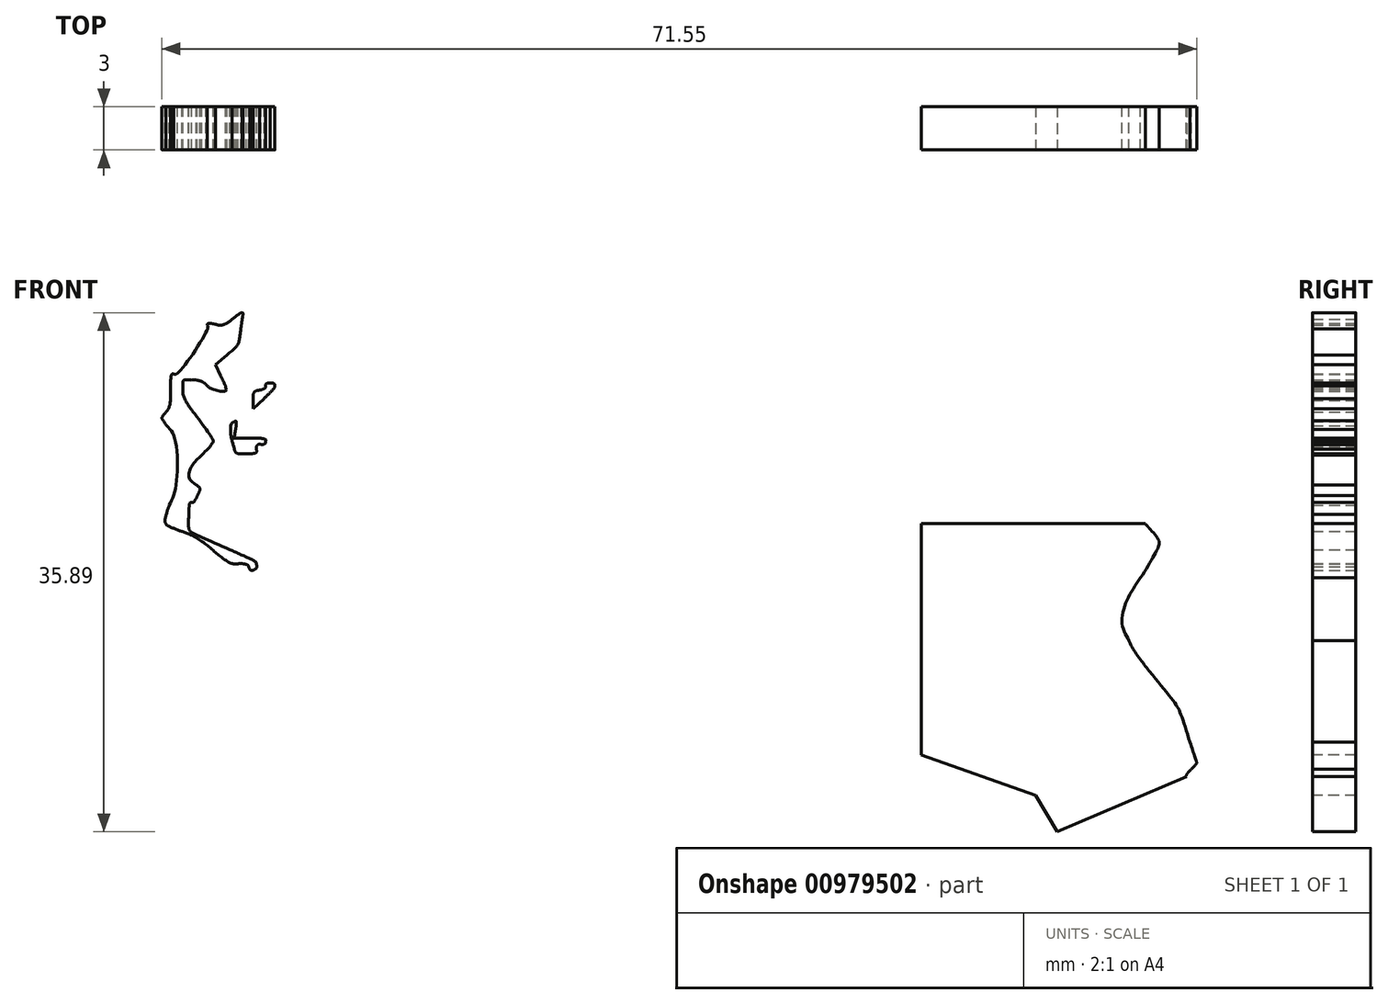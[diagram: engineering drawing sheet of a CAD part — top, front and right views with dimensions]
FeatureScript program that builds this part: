
annotation { "Feature Type Name" : "Feature", "Feature Type Description" : "" }
export const myFeature = defineFeature(function(context is Context, id is Id, definition is map)
    precondition{}
    {
        {
            var Q0;
            Q0=qCreatedBy(makeId("Front.planeOp"),FACE);
            var sketch = newSketch(context, id + "F0", { "sketchPlane" : qUnion([Q0])});
            skLineSegment(sketch, "E0", {"start": v(-32.88, 19.2) * mm, "end": v(-32.1, 20.83) * mm});
            skLineSegment(sketch, "E1", {"start": v(-32.1, 20.83) * mm, "end": v(-32.57, 22.16) * mm});
            skLineSegment(sketch, "E2", {"start": v(-27.5, 16.63) * mm, "end": v(-26.83, 16.28) * mm});
            skLineSegment(sketch, "E3", {"start": v(-26.83, 16.28) * mm, "end": v(-26.97, 16.83) * mm});
            skLineSegment(sketch, "E4", {"start": v(-24.85, 15.67) * mm, "end": v(-25.4, 15.88) * mm});
            skLineSegment(sketch, "E5", {"start": v(-25.4, 15.88) * mm, "end": v(-25.34, 18.4) * mm});
            skLineSegment(sketch, "E6", {"start": v(-1.75, 78.04) * mm, "end": v(-0.2, 79.6) * mm});
            skLineSegment(sketch, "E7", {"start": v(-0.2, 79.6) * mm, "end": v(1.27, 79.6) * mm});
            skLineSegment(sketch, "E8", {"start": v(38.3, 44.26) * mm, "end": v(38.3, 43.17) * mm});
            skLineSegment(sketch, "E9", {"start": v(38.3, 43.17) * mm, "end": v(37.62, 43.24) * mm});
            skLineSegment(sketch, "E10", {"start": v(39.65, -31.25) * mm, "end": v(39.52, -33.83) * mm});
            skLineSegment(sketch, "E11", {"start": v(39.52, -33.83) * mm, "end": v(40.18, -34.42) * mm});
            skLineSegment(sketch, "E12", {"start": v(1.4, 79.08) * mm, "end": v(0.3, 79.22) * mm});
            skLineSegment(sketch, "E13", {"start": v(0.3, 79.22) * mm, "end": v(-1.23, 77.67) * mm});
            skLineSegment(sketch, "E14", {"start": v(-12.51, 69.45) * mm, "end": v(-13.4, 69.45) * mm});
            skLineSegment(sketch, "E15", {"start": v(-13.4, 69.45) * mm, "end": v(-13.27, 67.07) * mm});
            skLineSegment(sketch, "E16", {"start": v(-18.31, 54.9) * mm, "end": v(-18.88, 53.48) * mm});
            skLineSegment(sketch, "E17", {"start": v(-18.88, 53.48) * mm, "end": v(-18.43, 53.1) * mm});
            skLineSegment(sketch, "E18", {"start": v(-20.94, 40.45) * mm, "end": v(-21.55, 40.45) * mm});
            skLineSegment(sketch, "E19", {"start": v(-21.55, 40.45) * mm, "end": v(-21.44, 41.8) * mm});
            skLineSegment(sketch, "E20", {"start": v(-24.47, 43.3) * mm, "end": v(-25.23, 42.61) * mm});
            skLineSegment(sketch, "E21", {"start": v(-25.23, 42.61) * mm, "end": v(-24.8, 41.05) * mm});
            skLineSegment(sketch, "E22", {"start": v(-37.96, -16.18) * mm, "end": v(-37.29, -17.23) * mm});
            skLineSegment(sketch, "E23", {"start": v(-37.29, -17.23) * mm, "end": v(-37.41, -20.41) * mm});
            skLineSegment(sketch, "E24", {"start": v(-30.4, -60.92) * mm, "end": v(-31.42, -62.04) * mm});
            skLineSegment(sketch, "E25", {"start": v(-31.42, -62.04) * mm, "end": v(-30.9, -63.02) * mm});
            skLineSegment(sketch, "E26", {"start": v(-36.35, 33.14) * mm, "end": v(-36.7, 33.88) * mm});
            skLineSegment(sketch, "E27", {"start": v(-36.7, 33.88) * mm, "end": v(-35.92, 34.57) * mm});
            skLineSegment(sketch, "E28", {"start": v(-34.09, 31.43) * mm, "end": v(-34.09, 30.84) * mm});
            skLineSegment(sketch, "E29", {"start": v(-34.09, 30.84) * mm, "end": v(-33.35, 31.56) * mm});
            skFitSpline(sketch, "E30", {"points": [v(-13.45, -80.7) * mm, v(-14.26, -80.4) * mm, v(-15.79, -79.86) * mm, v(-16.84, -79.51) * mm]});
            skFitSpline(sketch, "E31", {"points": [v(-16.84, -79.51) * mm, v(-20.43, -78.33) * mm, v(-20.6, -78.25) * mm, v(-21.55, -77.26) * mm]});
            skFitSpline(sketch, "E32", {"points": [v(-21.55, -77.26) * mm, v(-22.07, -76.72) * mm, v(-23.66, -74.52) * mm, v(-25.09, -72.37) * mm]});
            skFitSpline(sketch, "E33", {"points": [v(-25.09, -72.37) * mm, v(-26.52, -70.21) * mm, v(-28.36, -67.6) * mm, v(-29.19, -66.55) * mm]});
            skFitSpline(sketch, "E34", {"points": [v(-29.19, -66.55) * mm, v(-30.6, -64.76) * mm, v(-31.97, -62.53) * mm, v(-31.97, -62.03) * mm]});
            skFitSpline(sketch, "E35", {"points": [v(-31.97, -62.03) * mm, v(-31.97, -61.91) * mm, v(-31.5, -61.27) * mm, v(-30.92, -60.6) * mm]});
            skFitSpline(sketch, "E36", {"points": [v(-30.92, -60.6) * mm, v(-29.85, -59.39) * mm, v(-29, -57.92) * mm, v(-29, -57.28) * mm]});
            skFitSpline(sketch, "E37", {"points": [v(-29, -57.28) * mm, v(-29, -57.08) * mm, v(-29.34, -56.3) * mm, v(-29.75, -55.53) * mm]});
            skFitSpline(sketch, "E38", {"points": [v(-29.75, -55.53) * mm, v(-30.57, -53.98) * mm, v(-30.63, -53.57) * mm, v(-30.2, -52.72) * mm]});
            skFitSpline(sketch, "E39", {"points": [v(-30.2, -52.72) * mm, v(-29.95, -52.26) * mm, v(-29.92, -51.55) * mm, v(-30.04, -49.29) * mm]});
            skFitSpline(sketch, "E40", {"points": [v(-30.04, -49.29) * mm, v(-30.2, -46.13) * mm, v(-30.12, -46.32) * mm, v(-32.34, -43.6) * mm]});
            skFitSpline(sketch, "E41", {"points": [v(-32.34, -43.6) * mm, v(-32.83, -43) * mm, v(-33.38, -42.01) * mm, v(-33.55, -41.42) * mm]});
            skFitSpline(sketch, "E42", {"points": [v(-33.55, -41.42) * mm, v(-33.73, -40.84) * mm, v(-34.2, -39.94) * mm, v(-34.62, -39.44) * mm]});
            skFitSpline(sketch, "E43", {"points": [v(-34.62, -39.44) * mm, v(-36.03, -37.71) * mm, v(-36.52, -35.97) * mm, v(-35.98, -34.56) * mm]});
            skFitSpline(sketch, "E44", {"points": [v(-35.98, -34.56) * mm, v(-35.86, -34.24) * mm, v(-35.38, -33.57) * mm, v(-34.92, -33.07) * mm]});
            skFitSpline(sketch, "E45", {"points": [v(-34.92, -33.07) * mm, v(-33.97, -32.03) * mm, v(-34, -32.17) * mm, v(-34.37, -30.78) * mm]});
            skFitSpline(sketch, "E46", {"points": [v(-34.37, -30.78) * mm, v(-34.75, -29.38) * mm, v(-35.2, -28.53) * mm, v(-36.46, -26.88) * mm]});
            skFitSpline(sketch, "E47", {"points": [v(-36.46, -26.88) * mm, v(-37.04, -26.13) * mm, v(-37.61, -25.27) * mm, v(-37.73, -24.97) * mm]});
            skFitSpline(sketch, "E48", {"points": [v(-37.73, -24.97) * mm, v(-37.97, -24.39) * mm, v(-38.06, -21.07) * mm, v(-37.9, -18.8) * mm]});
            skFitSpline(sketch, "E49", {"points": [v(-37.9, -18.8) * mm, v(-37.82, -17.55) * mm, v(-37.87, -17.35) * mm, v(-38.39, -16.67) * mm]});
            skFitSpline(sketch, "E50", {"points": [v(-38.39, -16.67) * mm, v(-39.51, -15.19) * mm, v(-39.6, -12.77) * mm, v(-38.72, -7.81) * mm]});
            skFitSpline(sketch, "E51", {"points": [v(-38.72, -7.81) * mm, v(-38.24, -5.14) * mm, v(-38.31, -2.1) * mm, v(-38.87, -1) * mm]});
            skFitSpline(sketch, "E52", {"points": [v(-38.87, -1) * mm, v(-39.1, -0.56) * mm, v(-39.11, -0.29) * mm, v(-38.94, 0.17) * mm]});
            skFitSpline(sketch, "E53", {"points": [v(-38.94, 0.17) * mm, v(-38.62, 1) * mm, v(-38.87, 3.38) * mm, v(-39.5, 5.38) * mm]});
            skFitSpline(sketch, "E54", {"points": [v(-39.5, 5.38) * mm, v(-39.78, 6.29) * mm, v(-40.01, 7.26) * mm, v(-40.01, 7.54) * mm]});
            skFitSpline(sketch, "E55", {"points": [v(-40.01, 7.54) * mm, v(-40.01, 7.83) * mm, v(-39.68, 9.05) * mm, v(-39.27, 10.27) * mm]});
            skFitSpline(sketch, "E56", {"points": [v(-39.27, 10.27) * mm, v(-38.41, 12.85) * mm, v(-38.39, 13.06) * mm, v(-38.96, 13.2) * mm]});
            skFitSpline(sketch, "E57", {"points": [v(-38.96, 13.2) * mm, v(-39.71, 13.4) * mm, v(-39.48, 14.32) * mm, v(-38.38, 15.5) * mm]});
            skFitSpline(sketch, "E58", {"points": [v(-38.38, 15.5) * mm, v(-36.83, 17.16) * mm, v(-35.68, 17.57) * mm, v(-34.74, 16.8) * mm]});
            skFitSpline(sketch, "E59", {"points": [v(-34.74, 16.8) * mm, v(-34.08, 16.26) * mm, v(-32.77, 13.22) * mm, v(-32.66, 11.98) * mm]});
            skFitSpline(sketch, "E60", {"points": [v(-32.66, 11.98) * mm, v(-32.55, 10.86) * mm, v(-32.37, 10.61) * mm, v(-31.6, 10.6) * mm]});
            skFitSpline(sketch, "E61", {"points": [v(-31.6, 10.6) * mm, v(-31, 10.6) * mm, v(-30.96, 11.24) * mm, v(-31.55, 11.77) * mm]});
            skFitSpline(sketch, "E62", {"points": [v(-31.55, 11.77) * mm, v(-31.84, 12.03) * mm, v(-31.97, 12.42) * mm, v(-31.97, 13) * mm]});
            skFitSpline(sketch, "E63", {"points": [v(-31.97, 13) * mm, v(-31.97, 14.32) * mm, v(-32.62, 16.12) * mm, v(-33.18, 16.38) * mm]});
            skFitSpline(sketch, "E64", {"points": [v(-33.18, 16.38) * mm, v(-33.86, 16.69) * mm, v(-33.8, 17.27) * mm, v(-32.88, 19.2) * mm]});
            skFitSpline(sketch, "E65", {"points": [v(-32.57, 22.16) * mm, v(-32.82, 22.9) * mm, v(-33.03, 23.65) * mm, v(-33.03, 23.83) * mm]});
            skFitSpline(sketch, "E66", {"points": [v(-33.03, 23.83) * mm, v(-33.03, 24.1) * mm, v(-33.14, 24.14) * mm, v(-33.5, 24.01) * mm]});
            skFitSpline(sketch, "E67", {"points": [v(-33.5, 24.01) * mm, v(-33.77, 23.92) * mm, v(-34.4, 23.84) * mm, v(-34.93, 23.84) * mm]});
            skFitSpline(sketch, "E68", {"points": [v(-34.93, 23.84) * mm, v(-35.84, 23.83) * mm, v(-35.89, 23.86) * mm, v(-35.95, 24.48) * mm]});
            skFitSpline(sketch, "E69", {"points": [v(-35.95, 24.48) * mm, v(-36.05, 25.55) * mm, v(-34.78, 26.27) * mm, v(-32.78, 26.27) * mm]});
            skFitSpline(sketch, "E70", {"points": [v(-32.78, 26.27) * mm, v(-31.93, 26.27) * mm, v(-31.64, 26.16) * mm, v(-31.1, 25.65) * mm]});
            skFitSpline(sketch, "E71", {"points": [v(-31.1, 25.65) * mm, v(-30.75, 25.3) * mm, v(-30.32, 25.08) * mm, v(-30.15, 25.14) * mm]});
            skFitSpline(sketch, "E72", {"points": [v(-30.15, 25.14) * mm, v(-29.7, 25.31) * mm, v(-29.77, 25.47) * mm, v(-30.7, 26.37) * mm]});
            skFitSpline(sketch, "E73", {"points": [v(-30.7, 26.37) * mm, v(-31.5, 27.15) * mm, v(-31.55, 27.27) * mm, v(-31.55, 28.43) * mm]});
            skFitSpline(sketch, "E74", {"points": [v(-31.55, 28.43) * mm, v(-31.55, 29.6) * mm, v(-31.52, 29.65) * mm, v(-31.02, 29.65) * mm]});
            skFitSpline(sketch, "E75", {"points": [v(-31.02, 29.65) * mm, v(-30.7, 29.65) * mm, v(-30.49, 29.53) * mm, v(-30.49, 29.36) * mm]});
            skFitSpline(sketch, "E76", {"points": [v(-30.49, 29.36) * mm, v(-30.49, 28.94) * mm, v(-28.82, 27.75) * mm, v(-28.24, 27.75) * mm]});
            skFitSpline(sketch, "E77", {"points": [v(-28.24, 27.75) * mm, v(-27.83, 27.75) * mm, v(-27.75, 27.6) * mm, v(-27.62, 26.6) * mm]});
            skFitSpline(sketch, "E78", {"points": [v(-27.62, 26.6) * mm, v(-27.46, 25.26) * mm, v(-27.66, 24.55) * mm, v(-28.57, 23.22) * mm]});
            skFitSpline(sketch, "E79", {"points": [v(-28.57, 23.22) * mm, v(-29.21, 22.29) * mm, v(-29.4, 21.61) * mm, v(-29.02, 21.61) * mm]});
            skFitSpline(sketch, "E80", {"points": [v(-29.02, 21.61) * mm, v(-28.66, 21.61) * mm, v(-28.35, 20.18) * mm, v(-28.49, 19.14) * mm]});
            skFitSpline(sketch, "E81", {"points": [v(-28.49, 19.14) * mm, v(-28.66, 17.84) * mm, v(-28.36, 17.07) * mm, v(-27.5, 16.63) * mm]});
            skFitSpline(sketch, "E82", {"points": [v(-26.97, 16.83) * mm, v(-27.1, 17.33) * mm, v(-27.05, 17.38) * mm, v(-26.5, 17.38) * mm]});
            skFitSpline(sketch, "E83", {"points": [v(-26.5, 17.38) * mm, v(-25.81, 17.38) * mm, v(-25.62, 17.08) * mm, v(-25.62, 16.04) * mm]});
            skFitSpline(sketch, "E84", {"points": [v(-25.62, 16.04) * mm, v(-25.62, 15.5) * mm, v(-25.82, 15.19) * mm, v(-26.56, 14.52) * mm]});
            skFitSpline(sketch, "E85", {"points": [v(-26.56, 14.52) * mm, v(-27.09, 14.05) * mm, v(-27.58, 13.4) * mm, v(-27.66, 13.06) * mm]});
            skFitSpline(sketch, "E86", {"points": [v(-27.66, 13.06) * mm, v(-27.79, 12.49) * mm, v(-27.76, 12.45) * mm, v(-27.3, 12.58) * mm]});
            skFitSpline(sketch, "E87", {"points": [v(-27.3, 12.58) * mm, v(-27.01, 12.65) * mm, v(-26.47, 12.72) * mm, v(-26.09, 12.72) * mm]});
            skFitSpline(sketch, "E88", {"points": [v(-26.09, 12.72) * mm, v(-25.47, 12.72) * mm, v(-25.42, 12.76) * mm, v(-25.61, 13.13) * mm]});
            skFitSpline(sketch, "E89", {"points": [v(-25.61, 13.13) * mm, v(-26.02, 13.88) * mm, v(-25.88, 14.6) * mm, v(-25.31, 14.75) * mm]});
            skFitSpline(sketch, "E90", {"points": [v(-25.31, 14.75) * mm, v(-25.03, 14.82) * mm, v(-24.68, 15.01) * mm, v(-24.55, 15.17) * mm]});
            skFitSpline(sketch, "E91", {"points": [v(-24.55, 15.17) * mm, v(-24.35, 15.4) * mm, v(-24.42, 15.5) * mm, v(-24.85, 15.67) * mm]});
            skFitSpline(sketch, "E92", {"points": [v(-25.34, 18.4) * mm, v(-25.28, 20.49) * mm, v(-25.2, 21.05) * mm, v(-24.84, 21.66) * mm]});
            skFitSpline(sketch, "E93", {"points": [v(-24.84, 21.66) * mm, v(-24.6, 22.07) * mm, v(-24.33, 22.91) * mm, v(-24.25, 23.54) * mm]});
            skFitSpline(sketch, "E94", {"points": [v(-24.25, 23.54) * mm, v(-24.05, 24.98) * mm, v(-23.67, 25.42) * mm, v(-22.64, 25.42) * mm]});
            skFitSpline(sketch, "E95", {"points": [v(-22.64, 25.42) * mm, v(-21.97, 25.42) * mm, v(-21.73, 25.28) * mm, v(-21.09, 24.54) * mm]});
            skFitSpline(sketch, "E96", {"points": [v(-21.09, 24.54) * mm, v(-20.67, 24.05) * mm, v(-20.32, 23.55) * mm, v(-20.32, 23.43) * mm]});
            skFitSpline(sketch, "E97", {"points": [v(-20.32, 23.43) * mm, v(-20.3, 22.93) * mm, v(-19.5, 25.15) * mm, v(-19.5, 25.74) * mm]});
            skFitSpline(sketch, "E98", {"points": [v(-19.5, 25.74) * mm, v(-19.48, 26.68) * mm, v(-19.75, 27) * mm, v(-20.27, 26.68) * mm]});
            skFitSpline(sketch, "E99", {"points": [v(-20.27, 26.68) * mm, v(-20.84, 26.32) * mm, v(-23.7, 26.75) * mm, v(-24.99, 27.38) * mm]});
            skFitSpline(sketch, "E100", {"points": [v(-24.99, 27.38) * mm, v(-26.7, 28.23) * mm, v(-27.27, 29.95) * mm, v(-26.55, 32.07) * mm]});
            skFitSpline(sketch, "E101", {"points": [v(-26.55, 32.07) * mm, v(-26.23, 33) * mm, v(-26.23, 33.13) * mm, v(-26.58, 33.9) * mm]});
            skFitSpline(sketch, "E102", {"points": [v(-26.58, 33.9) * mm, v(-27.04, 34.91) * mm, v(-26.9, 36) * mm, v(-26.2, 36.92) * mm]});
            skFitSpline(sketch, "E103", {"points": [v(-26.2, 36.92) * mm, v(-24.96, 38.54) * mm, v(-24.76, 39.42) * mm, v(-25.3, 40.73) * mm]});
            skFitSpline(sketch, "E104", {"points": [v(-25.3, 40.73) * mm, v(-25.48, 41.15) * mm, v(-25.62, 41.87) * mm, v(-25.62, 42.33) * mm]});
            skFitSpline(sketch, "E105", {"points": [v(-25.62, 42.33) * mm, v(-25.62, 43.02) * mm, v(-25.5, 43.25) * mm, v(-24.99, 43.62) * mm]});
            skFitSpline(sketch, "E106", {"points": [v(-24.99, 43.62) * mm, v(-24.64, 43.87) * mm, v(-24.35, 44.26) * mm, v(-24.35, 44.48) * mm]});
            skFitSpline(sketch, "E107", {"points": [v(-24.35, 44.48) * mm, v(-24.35, 45.6) * mm, v(-22.43, 46.16) * mm, v(-21.62, 45.29) * mm]});
            skFitSpline(sketch, "E108", {"points": [v(-21.62, 45.29) * mm, v(-21.1, 44.74) * mm, v(-20.66, 42.78) * mm, v(-20.82, 41.8) * mm]});
            skFitSpline(sketch, "E109", {"points": [v(-20.82, 41.8) * mm, v(-20.95, 40.98) * mm, v(-20.5, 40.8) * mm, v(-20.12, 41.5) * mm]});
            skFitSpline(sketch, "E110", {"points": [v(-20.12, 41.5) * mm, v(-20, 41.74) * mm, v(-19.7, 41.93) * mm, v(-19.48, 41.93) * mm]});
            skFitSpline(sketch, "E111", {"points": [v(-19.48, 41.93) * mm, v(-19.2, 41.93) * mm, v(-19.03, 42.12) * mm, v(-18.95, 42.51) * mm]});
            skFitSpline(sketch, "E112", {"points": [v(-18.95, 42.51) * mm, v(-18.9, 42.83) * mm, v(-18.75, 43.5) * mm, v(-18.63, 44) * mm]});
            skFitSpline(sketch, "E113", {"points": [v(-18.63, 44) * mm, v(-18.15, 46.1) * mm, v(-18.46, 46.83) * mm, v(-19.95, 47.1) * mm]});
            skFitSpline(sketch, "E114", {"points": [v(-19.95, 47.1) * mm, v(-21.37, 47.35) * mm, v(-21.68, 48.31) * mm, v(-21.02, 50.45) * mm]});
            skFitSpline(sketch, "E115", {"points": [v(-21.02, 50.45) * mm, v(-20.67, 51.58) * mm, v(-20.6, 51.66) * mm, v(-20, 51.67) * mm]});
            skFitSpline(sketch, "E116", {"points": [v(-20, 51.67) * mm, v(-19.64, 51.67) * mm, v(-19.17, 51.8) * mm, v(-18.94, 51.97) * mm]});
            skFitSpline(sketch, "E117", {"points": [v(-18.94, 51.97) * mm, v(-18.56, 52.25) * mm, v(-18.55, 52.28) * mm, v(-18.9, 52.67) * mm]});
            skFitSpline(sketch, "E118", {"points": [v(-18.9, 52.67) * mm, v(-19.36, 53.18) * mm, v(-19.37, 53.99) * mm, v(-18.93, 55) * mm]});
            skFitSpline(sketch, "E119", {"points": [v(-18.93, 55) * mm, v(-18.26, 56.57) * mm, v(-18.22, 56.96) * mm, v(-18.55, 58.71) * mm]});
            skFitSpline(sketch, "E120", {"points": [v(-18.55, 58.71) * mm, v(-19.05, 61.35) * mm, v(-18.66, 63.1) * mm, v(-17.57, 63.1) * mm]});
            skFitSpline(sketch, "E121", {"points": [v(-17.57, 63.1) * mm, v(-17.13, 63.1) * mm, v(-16.93, 62.86) * mm, v(-16.62, 61.94) * mm]});
            skFitSpline(sketch, "E122", {"points": [v(-16.62, 61.94) * mm, v(-16.19, 60.62) * mm, v(-15.25, 61.36) * mm, v(-15.25, 63.03) * mm]});
            skFitSpline(sketch, "E123", {"points": [v(-15.25, 63.03) * mm, v(-15.25, 63.72) * mm, v(-15.21, 63.77) * mm, v(-14.72, 63.65) * mm]});
            skFitSpline(sketch, "E124", {"points": [v(-14.72, 63.65) * mm, v(-13.88, 63.44) * mm, v(-13.7, 64.21) * mm, v(-13.86, 67.25) * mm]});
            skFitSpline(sketch, "E125", {"points": [v(-13.86, 67.25) * mm, v(-14.01, 70.15) * mm, v(-14.06, 70.07) * mm, v(-12.21, 70.08) * mm]});
            skFitSpline(sketch, "E126", {"points": [v(-12.21, 70.08) * mm, v(-11.52, 70.08) * mm, v(-11.25, 70.23) * mm, v(-10.4, 71.12) * mm]});
            skFitSpline(sketch, "E127", {"points": [v(-10.4, 71.12) * mm, v(-9.38, 72.18) * mm, v(-9.03, 72.34) * mm, v(-6.52, 72.84) * mm]});
            skFitSpline(sketch, "E128", {"points": [v(-6.52, 72.84) * mm, v(-4.93, 73.15) * mm, v(-4.21, 73.78) * mm, v(-3.7, 75.27) * mm]});
            skFitSpline(sketch, "E129", {"points": [v(-3.7, 75.27) * mm, v(-3.38, 76.2) * mm, v(-2.96, 76.8) * mm, v(-1.75, 78.04) * mm]});
            skFitSpline(sketch, "E130", {"points": [v(1.27, 79.6) * mm, v(2.66, 79.6) * mm, v(2.79, 79.65) * mm, v(3.57, 80.36) * mm]});
            skFitSpline(sketch, "E131", {"points": [v(3.57, 80.36) * mm, v(4.72, 81.4) * mm, v(5.62, 81.51) * mm, v(6.84, 80.8) * mm]});
            skFitSpline(sketch, "E132", {"points": [v(6.84, 80.8) * mm, v(7.4, 80.48) * mm, v(8.11, 80.24) * mm, v(8.56, 80.24) * mm]});
            skFitSpline(sketch, "E133", {"points": [v(8.56, 80.24) * mm, v(9.65, 80.24) * mm, v(10.66, 79.76) * mm, v(12.03, 78.58) * mm]});
            skFitSpline(sketch, "E134", {"points": [v(12.03, 78.58) * mm, v(12.68, 78.02) * mm, v(13.76, 77.21) * mm, v(14.43, 76.8) * mm]});
            skFitSpline(sketch, "E135", {"points": [v(14.43, 76.8) * mm, v(16.07, 75.75) * mm, v(16.3, 75.23) * mm, v(16.26, 72.68) * mm]});
            skFitSpline(sketch, "E136", {"points": [v(16.26, 72.68) * mm, v(16.21, 70.3) * mm, v(16.3, 70.06) * mm, v(17.99, 67.97) * mm]});
            skFitSpline(sketch, "E137", {"points": [v(17.99, 67.97) * mm, v(19.34, 66.28) * mm, v(19.58, 65.73) * mm, v(19.78, 63.84) * mm]});
            skFitSpline(sketch, "E138", {"points": [v(19.78, 63.84) * mm, v(19.97, 61.97) * mm, v(20.1, 61.75) * mm, v(21.2, 61.28) * mm]});
            skFitSpline(sketch, "E139", {"points": [v(21.2, 61.28) * mm, v(21.95, 60.97) * mm, v(22.77, 60.9) * mm, v(25.95, 60.87) * mm]});
            skFitSpline(sketch, "E140", {"points": [v(25.95, 60.87) * mm, v(29.47, 60.83) * mm, v(29.87, 60.8) * mm, v(30.78, 60.35) * mm]});
            skFitSpline(sketch, "E141", {"points": [v(30.78, 60.35) * mm, v(31.33, 60.09) * mm, v(31.82, 59.71) * mm, v(31.88, 59.53) * mm]});
            skFitSpline(sketch, "E142", {"points": [v(31.88, 59.53) * mm, v(32.1, 58.78) * mm, v(32.32, 58.58) * mm, v(33.34, 58.19) * mm]});
            skFitSpline(sketch, "E143", {"points": [v(33.34, 58.19) * mm, v(35, 57.54) * mm, v(35.47, 56.96) * mm, v(35.61, 55.41) * mm]});
            skFitSpline(sketch, "E144", {"points": [v(35.61, 55.41) * mm, v(35.68, 54.7) * mm, v(35.93, 53.67) * mm, v(36.17, 53.15) * mm]});
            skFitSpline(sketch, "E145", {"points": [v(36.17, 53.15) * mm, v(36.4, 52.63) * mm, v(36.6, 51.94) * mm, v(36.6, 51.62) * mm]});
            skFitSpline(sketch, "E146", {"points": [v(36.6, 51.62) * mm, v(36.6, 51.3) * mm, v(36.8, 50.55) * mm, v(37.02, 49.93) * mm]});
            skFitSpline(sketch, "E147", {"points": [v(37.02, 49.93) * mm, v(37.7, 48.08) * mm, v(38.3, 45.42) * mm, v(38.3, 44.26) * mm]});
            skFitSpline(sketch, "E148", {"points": [v(37.62, 43.24) * mm, v(36.87, 43.31) * mm, v(36.86, 43.33) * mm, v(36.05, 46.9) * mm]});
            skFitSpline(sketch, "E149", {"points": [v(36.05, 46.9) * mm, v(35.75, 48.23) * mm, v(35.65, 48.45) * mm, v(35.6, 47.92) * mm]});
            skFitSpline(sketch, "E150", {"points": [v(35.6, 47.92) * mm, v(35.56, 47.55) * mm, v(35.72, 46.61) * mm, v(35.96, 45.84) * mm]});
            skFitSpline(sketch, "E151", {"points": [v(35.96, 45.84) * mm, v(36.2, 45.06) * mm, v(36.4, 44.16) * mm, v(36.4, 43.83) * mm]});
            skFitSpline(sketch, "E152", {"points": [v(36.4, 43.83) * mm, v(36.4, 42.72) * mm, v(36.23, 42.57) * mm, v(35.04, 42.57) * mm]});
            skFitSpline(sketch, "E153", {"points": [v(35.04, 42.57) * mm, v(34.35, 42.57) * mm, v(33.78, 42.44) * mm, v(33.53, 42.23) * mm]});
            skFitSpline(sketch, "E154", {"points": [v(33.53, 42.23) * mm, v(33.14, 41.92) * mm, v(33.15, 41.9) * mm, v(33.78, 42.01) * mm]});
            skFitSpline(sketch, "E155", {"points": [v(33.78, 42.01) * mm, v(34.37, 42.1) * mm, v(34.48, 42.05) * mm, v(34.7, 41.5) * mm]});
            skFitSpline(sketch, "E156", {"points": [v(34.7, 41.5) * mm, v(35.23, 40.23) * mm, v(34.46, 39.89) * mm, v(32.77, 40.66) * mm]});
            skFitSpline(sketch, "E157", {"points": [v(32.77, 40.66) * mm, v(30, 41.91) * mm, v(30.46, 40.26) * mm, v(33.3, 38.77) * mm]});
            skFitSpline(sketch, "E158", {"points": [v(33.3, 38.77) * mm, v(34.7, 38.04) * mm, v(35.03, 37.98) * mm, v(35.2, 38.44) * mm]});
            skFitSpline(sketch, "E159", {"points": [v(35.2, 38.44) * mm, v(35.4, 38.97) * mm, v(36.94, 38.86) * mm, v(37.34, 38.29) * mm]});
            skFitSpline(sketch, "E160", {"points": [v(37.34, 38.29) * mm, v(37.8, 37.64) * mm, v(37.75, 36.5) * mm, v(37.25, 35.69) * mm]});
            skFitSpline(sketch, "E161", {"points": [v(37.25, 35.69) * mm, v(37.01, 35.31) * mm, v(36.68, 34.6) * mm, v(36.5, 34.09) * mm]});
            skFitSpline(sketch, "E162", {"points": [v(36.5, 34.09) * mm, v(36.07, 32.87) * mm, v(35.62, 32.4) * mm, v(34.86, 32.4) * mm]});
            skFitSpline(sketch, "E163", {"points": [v(34.86, 32.4) * mm, v(34.06, 32.4) * mm, v(32.85, 32.98) * mm, v(32.57, 33.5) * mm]});
            skFitSpline(sketch, "E164", {"points": [v(32.57, 33.5) * mm, v(32.35, 33.9) * mm, v(32.37, 33.91) * mm, v(33.4, 34.23) * mm]});
            skFitSpline(sketch, "E165", {"points": [v(33.4, 34.23) * mm, v(33.55, 34.27) * mm, v(33.64, 34.43) * mm, v(33.6, 34.58) * mm]});
            skFitSpline(sketch, "E166", {"points": [v(33.6, 34.58) * mm, v(33.47, 34.97) * mm, v(32.1, 35.02) * mm, v(31.26, 34.66) * mm]});
            skFitSpline(sketch, "E167", {"points": [v(31.26, 34.66) * mm, v(30.63, 34.4) * mm, v(30.54, 34.27) * mm, v(30.63, 33.8) * mm]});
            skFitSpline(sketch, "E168", {"points": [v(30.63, 33.8) * mm, v(30.71, 33.37) * mm, v(30.83, 33.27) * mm, v(31.13, 33.37) * mm]});
            skFitSpline(sketch, "E169", {"points": [v(31.13, 33.37) * mm, v(31.68, 33.54) * mm, v(31.8, 33.13) * mm, v(31.57, 31.7) * mm]});
            skFitSpline(sketch, "E170", {"points": [v(31.57, 31.7) * mm, v(31.47, 31.04) * mm, v(31.4, 30.5) * mm, v(31.43, 30.5) * mm]});
            skFitSpline(sketch, "E171", {"points": [v(31.43, 30.5) * mm, v(31.46, 30.5) * mm, v(31.82, 30.65) * mm, v(32.25, 30.82) * mm]});
            skFitSpline(sketch, "E172", {"points": [v(32.25, 30.82) * mm, v(33.01, 31.14) * mm, v(33.02, 31.14) * mm, v(33.26, 30.56) * mm]});
            skFitSpline(sketch, "E173", {"points": [v(33.26, 30.56) * mm, v(33.39, 30.24) * mm, v(33.5, 29.43) * mm, v(33.52, 28.77) * mm]});
            skFitSpline(sketch, "E174", {"points": [v(33.52, 28.77) * mm, v(33.55, 27.14) * mm, v(33.03, 26.57) * mm, v(31.4, 26.43) * mm]});
            skFitSpline(sketch, "E175", {"points": [v(31.4, 26.43) * mm, v(29.99, 26.32) * mm, v(29.27, 25.83) * mm, v(28.59, 24.5) * mm]});
            skFitSpline(sketch, "E176", {"points": [v(28.59, 24.5) * mm, v(28.09, 23.52) * mm, v(28.09, 23.5) * mm, v(28.46, 22.8) * mm]});
            skFitSpline(sketch, "E177", {"points": [v(28.46, 22.8) * mm, v(29.02, 21.76) * mm, v(28.8, 20.5) * mm, v(27.76, 18.77) * mm]});
            skFitSpline(sketch, "E178", {"points": [v(27.76, 18.77) * mm, v(26.26, 16.28) * mm, v(26.34, 15.6) * mm, v(28.5, 12.89) * mm]});
            skFitSpline(sketch, "E179", {"points": [v(28.5, 12.89) * mm, v(30.07, 10.9) * mm, v(30.64, 9.85) * mm, v(31.32, 7.7) * mm]});
            skFitSpline(sketch, "E180", {"points": [v(31.32, 7.7) * mm, v(31.79, 6.2) * mm, v(31.8, 6.14) * mm, v(31.41, 5.73) * mm]});
            skFitSpline(sketch, "E181", {"points": [v(31.41, 5.73) * mm, v(31.08, 5.36) * mm, v(31.06, 5.2) * mm, v(31.28, 4.6) * mm]});
            skFitSpline(sketch, "E182", {"points": [v(31.28, 4.6) * mm, v(31.65, 3.58) * mm, v(31.59, 2.92) * mm, v(31, 1.59) * mm]});
            skFitSpline(sketch, "E183", {"points": [v(31, 1.59) * mm, v(30.4, 0.22) * mm, v(30.37, 0) * mm, v(30.73, -0.98) * mm]});
            skFitSpline(sketch, "E184", {"points": [v(30.73, -0.98) * mm, v(30.96, -1.6) * mm, v(30.93, -1.79) * mm, v(30.48, -2.62) * mm]});
            skFitSpline(sketch, "E185", {"points": [v(30.48, -2.62) * mm, v(29.76, -3.92) * mm, v(30.03, -4.4) * mm, v(31.97, -5.39) * mm]});
            skFitSpline(sketch, "E186", {"points": [v(31.97, -5.39) * mm, v(33.32, -6.07) * mm, v(33.55, -6.12) * mm, v(34.1, -5.9) * mm]});
            skFitSpline(sketch, "E187", {"points": [v(34.1, -5.9) * mm, v(34.89, -5.57) * mm, v(35.48, -5.74) * mm, v(36.67, -6.64) * mm]});
            skFitSpline(sketch, "E188", {"points": [v(36.67, -6.64) * mm, v(37.21, -7.06) * mm, v(37.94, -7.45) * mm, v(38.28, -7.52) * mm]});
            skFitSpline(sketch, "E189", {"points": [v(38.28, -7.52) * mm, v(38.74, -7.61) * mm, v(38.97, -7.82) * mm, v(39.14, -8.29) * mm]});
            skFitSpline(sketch, "E190", {"points": [v(39.14, -8.29) * mm, v(39.46, -9.22) * mm, v(39.43, -9.36) * mm, v(38.73, -10.24) * mm]});
            skFitSpline(sketch, "E191", {"points": [v(38.73, -10.24) * mm, v(37.95, -11.22) * mm, v(37.9, -12.13) * mm, v(38.57, -13.12) * mm]});
            skFitSpline(sketch, "E192", {"points": [v(38.57, -13.12) * mm, v(38.94, -13.67) * mm, v(39.23, -13.86) * mm, v(39.79, -13.91) * mm]});
            skFitSpline(sketch, "E193", {"points": [v(39.79, -13.91) * mm, v(40.2, -13.95) * mm, v(40.6, -14.1) * mm, v(40.68, -14.23) * mm]});
            skFitSpline(sketch, "E194", {"points": [v(40.68, -14.23) * mm, v(40.98, -14.7) * mm, v(40.84, -15.58) * mm, v(40.4, -15.98) * mm]});
            skFitSpline(sketch, "E195", {"points": [v(40.4, -15.98) * mm, v(40.04, -16.3) * mm, v(39.97, -16.56) * mm, v(40.05, -17.26) * mm]});
            skFitSpline(sketch, "E196", {"points": [v(40.05, -17.26) * mm, v(40.14, -18.03) * mm, v(40.09, -18.17) * mm, v(39.65, -18.37) * mm]});
            skFitSpline(sketch, "E197", {"points": [v(39.65, -18.37) * mm, v(39.06, -18.64) * mm, v(39.03, -18.9) * mm, v(39.5, -20) * mm]});
            skFitSpline(sketch, "E198", {"points": [v(39.5, -20) * mm, v(39.77, -20.67) * mm, v(39.83, -21.57) * mm, v(39.81, -24.74) * mm]});
            skFitSpline(sketch, "E199", {"points": [v(39.81, -24.74) * mm, v(39.8, -26.9) * mm, v(39.73, -29.82) * mm, v(39.65, -31.25) * mm]});
            skFitSpline(sketch, "E200", {"points": [v(40.18, -34.42) * mm, v(40.54, -34.74) * mm, v(40.84, -35.18) * mm, v(40.84, -35.41) * mm]});
            skFitSpline(sketch, "E201", {"points": [v(40.84, -35.41) * mm, v(40.84, -36.27) * mm, v(39.96, -37.65) * mm, v(38.92, -38.41) * mm]});
            skFitSpline(sketch, "E202", {"points": [v(38.92, -38.41) * mm, v(37.63, -39.36) * mm, v(37.28, -40) * mm, v(37.05, -41.89) * mm]});
            skFitSpline(sketch, "E203", {"points": [v(37.05, -41.89) * mm, v(36.94, -42.7) * mm, v(36.66, -43.77) * mm, v(36.42, -44.27) * mm]});
            skFitSpline(sketch, "E204", {"points": [v(36.42, -44.27) * mm, v(35.96, -45.22) * mm, v(33.78, -47.87) * mm, v(31.3, -50.5) * mm]});
            skFitSpline(sketch, "E205", {"points": [v(31.3, -50.5) * mm, v(29.02, -52.92) * mm, v(27.8, -55.66) * mm, v(27.2, -59.77) * mm]});
            skFitSpline(sketch, "E206", {"points": [v(27.2, -59.77) * mm, v(26.85, -62.13) * mm, v(26.75, -62.37) * mm, v(25.14, -65) * mm]});
            skFitSpline(sketch, "E207", {"points": [v(25.14, -65) * mm, v(24.58, -65.91) * mm, v(24.35, -66.6) * mm, v(24.16, -67.9) * mm]});
            skFitSpline(sketch, "E208", {"points": [v(24.16, -67.9) * mm, v(23.88, -69.93) * mm, v(23.36, -71.03) * mm, v(22.29, -71.92) * mm]});
            skFitSpline(sketch, "E209", {"points": [v(22.29, -71.92) * mm, v(21.43, -72.63) * mm, v(19.94, -73.22) * mm, v(19, -73.22) * mm]});
            skFitSpline(sketch, "E210", {"points": [v(19, -73.22) * mm, v(18.6, -73.22) * mm, v(18.4, -73.32) * mm, v(18.4, -73.56) * mm]});
            skFitSpline(sketch, "E211", {"points": [v(18.4, -73.56) * mm, v(18.4, -73.75) * mm, v(18.21, -74.22) * mm, v(17.97, -74.6) * mm]});
            skFitSpline(sketch, "E212", {"points": [v(17.97, -74.6) * mm, v(17.57, -75.26) * mm, v(17.56, -75.35) * mm, v(17.87, -76.08) * mm]});
            skFitSpline(sketch, "E213", {"points": [v(17.87, -76.08) * mm, v(18.34, -77.22) * mm, v(18.3, -77.38) * mm, v(17.14, -78.58) * mm]});
            skFitSpline(sketch, "E214", {"points": [v(17.14, -78.58) * mm, v(16.56, -79.18) * mm, v(15.87, -79.93) * mm, v(15.6, -80.25) * mm]});
            skFitSpline(sketch, "E215", {"points": [v(15.6, -80.25) * mm, v(15.34, -80.56) * mm, v(14.86, -80.88) * mm, v(14.54, -80.96) * mm]});
            skFitSpline(sketch, "E216", {"points": [v(14.54, -80.96) * mm, v(14.03, -81.08) * mm, v(13.96, -81.03) * mm, v(13.96, -80.56) * mm]});
            skFitSpline(sketch, "E217", {"points": [v(13.96, -80.56) * mm, v(13.96, -80.25) * mm, v(13.75, -79.86) * mm, v(13.47, -79.63) * mm]});
            skFitSpline(sketch, "E218", {"points": [v(13.47, -79.63) * mm, v(12.33, -78.73) * mm, v(12.3, -77.45) * mm, v(13.44, -77.45) * mm]});
            skFitSpline(sketch, "E219", {"points": [v(13.44, -77.45) * mm, v(14.2, -77.45) * mm, v(15.11, -76) * mm, v(14.94, -75.07) * mm]});
            skFitSpline(sketch, "E220", {"points": [v(14.94, -75.07) * mm, v(14.87, -74.7) * mm, v(14.75, -74.02) * mm, v(14.67, -73.57) * mm]});
            skFitSpline(sketch, "E221", {"points": [v(14.67, -73.57) * mm, v(14.58, -73.02) * mm, v(14.45, -72.8) * mm, v(14.25, -72.88) * mm]});
            skFitSpline(sketch, "E222", {"points": [v(14.25, -72.88) * mm, v(14.1, -72.94) * mm, v(13.13, -72.88) * mm, v(12.11, -72.76) * mm]});
            skFitSpline(sketch, "E223", {"points": [v(12.11, -72.76) * mm, v(10.8, -72.6) * mm, v(10.12, -72.4) * mm, v(9.8, -72.1) * mm]});
            skFitSpline(sketch, "E224", {"points": [v(9.8, -72.1) * mm, v(9.32, -71.67) * mm, v(8.88, -71.75) * mm, v(8.88, -72.28) * mm]});
            skFitSpline(sketch, "E225", {"points": [v(8.88, -72.28) * mm, v(8.88, -72.66) * mm, v(8.5, -72.65) * mm, v(7.82, -72.26) * mm]});
            skFitSpline(sketch, "E226", {"points": [v(7.82, -72.26) * mm, v(7.11, -71.86) * mm, v(5.83, -71.87) * mm, v(4.94, -72.29) * mm]});
            skFitSpline(sketch, "E227", {"points": [v(4.94, -72.29) * mm, v(4.16, -72.66) * mm, v(4.18, -72.61) * mm, v(4.14, -74.27) * mm]});
            skFitSpline(sketch, "E228", {"points": [v(4.14, -74.27) * mm, v(4.12, -75.43) * mm, v(4.11, -75.44) * mm, v(3.17, -75.91) * mm]});
            skFitSpline(sketch, "E229", {"points": [v(3.17, -75.91) * mm, v(2.65, -76.18) * mm, v(1.84, -76.77) * mm, v(1.36, -77.24) * mm]});
            skFitSpline(sketch, "E230", {"points": [v(1.36, -77.24) * mm, v(0.68, -77.91) * mm, v(-0.19, -78.37) * mm, v(-2.67, -79.37) * mm]});
            skFitSpline(sketch, "E231", {"points": [v(-2.67, -79.37) * mm, v(-6.5, -80.92) * mm, v(-7.82, -81.25) * mm, v(-10.17, -81.25) * mm]});
            skFitSpline(sketch, "E232", {"points": [v(-10.17, -81.25) * mm, v(-11.59, -81.25) * mm, v(-12.28, -81.13) * mm, v(-13.45, -80.7) * mm]});
            skFitSpline(sketch, "E233", {"points": [v(-6.84, -80.3) * mm, v(-6.29, -80.14) * mm, v(-4.56, -79.5) * mm, v(-3, -78.88) * mm]});
            skFitSpline(sketch, "E234", {"points": [v(-3, -78.88) * mm, v(-0.66, -77.96) * mm, v(0.05, -77.57) * mm, v(1.08, -76.65) * mm]});
            skFitSpline(sketch, "E235", {"points": [v(1.08, -76.65) * mm, v(1.77, -76.04) * mm, v(2.46, -75.54) * mm, v(2.62, -75.54) * mm]});
            skFitSpline(sketch, "E236", {"points": [v(2.62, -75.54) * mm, v(2.78, -75.54) * mm, v(3.12, -75.37) * mm, v(3.38, -75.16) * mm]});
            skFitSpline(sketch, "E237", {"points": [v(3.38, -75.16) * mm, v(3.8, -74.81) * mm, v(3.83, -74.72) * mm, v(3.59, -73.93) * mm]});
            skFitSpline(sketch, "E238", {"points": [v(3.59, -73.93) * mm, v(3.4, -73.28) * mm, v(3.39, -72.96) * mm, v(3.57, -72.61) * mm]});
            skFitSpline(sketch, "E239", {"points": [v(3.57, -72.61) * mm, v(4.07, -71.69) * mm, v(6.12, -71.11) * mm, v(7.53, -71.5) * mm]});
            skFitSpline(sketch, "E240", {"points": [v(7.53, -71.5) * mm, v(8.17, -71.68) * mm, v(8.4, -71.66) * mm, v(8.68, -71.41) * mm]});
            skFitSpline(sketch, "E241", {"points": [v(8.68, -71.41) * mm, v(9.15, -70.98) * mm, v(9.64, -71.02) * mm, v(10.13, -71.54) * mm]});
            skFitSpline(sketch, "E242", {"points": [v(10.13, -71.54) * mm, v(10.44, -71.88) * mm, v(10.95, -72.03) * mm, v(12.2, -72.17) * mm]});
            skFitSpline(sketch, "E243", {"points": [v(12.2, -72.17) * mm, v(13.1, -72.28) * mm, v(14, -72.32) * mm, v(14.17, -72.26) * mm]});
            skFitSpline(sketch, "E244", {"points": [v(14.17, -72.26) * mm, v(14.75, -72.09) * mm, v(15.04, -72.5) * mm, v(15.33, -73.91) * mm]});
            skFitSpline(sketch, "E245", {"points": [v(15.33, -73.91) * mm, v(15.54, -74.89) * mm, v(15.57, -75.53) * mm, v(15.43, -76.04) * mm]});
            skFitSpline(sketch, "E246", {"points": [v(15.43, -76.04) * mm, v(15.14, -77.06) * mm, v(14.45, -77.87) * mm, v(13.85, -77.87) * mm]});
            skFitSpline(sketch, "E247", {"points": [v(13.85, -77.87) * mm, v(13.06, -77.87) * mm, v(13.01, -78.27) * mm, v(13.7, -79) * mm]});
            skFitSpline(sketch, "E248", {"points": [v(13.7, -79) * mm, v(14.06, -79.37) * mm, v(14.38, -79.86) * mm, v(14.43, -80.1) * mm]});
            skFitSpline(sketch, "E249", {"points": [v(14.43, -80.1) * mm, v(14.5, -80.48) * mm, v(14.55, -80.47) * mm, v(15.03, -79.9) * mm]});
            skFitSpline(sketch, "E250", {"points": [v(15.03, -79.9) * mm, v(15.31, -79.57) * mm, v(16.02, -78.83) * mm, v(16.6, -78.28) * mm]});
            skFitSpline(sketch, "E251", {"points": [v(16.6, -78.28) * mm, v(17.64, -77.28) * mm, v(17.65, -77.26) * mm, v(17.4, -76.55) * mm]});
            skFitSpline(sketch, "E252", {"points": [v(17.4, -76.55) * mm, v(17.05, -75.6) * mm, v(17.07, -74.87) * mm, v(17.45, -74.37) * mm]});
            skFitSpline(sketch, "E253", {"points": [v(17.45, -74.37) * mm, v(17.62, -74.14) * mm, v(17.76, -73.7) * mm, v(17.76, -73.4) * mm]});
            skFitSpline(sketch, "E254", {"points": [v(17.76, -73.4) * mm, v(17.77, -72.89) * mm, v(17.86, -72.83) * mm, v(18.88, -72.7) * mm]});
            skFitSpline(sketch, "E255", {"points": [v(18.88, -72.7) * mm, v(19.5, -72.62) * mm, v(20.47, -72.3) * mm, v(21.04, -71.99) * mm]});
            skFitSpline(sketch, "E256", {"points": [v(21.04, -71.99) * mm, v(22.45, -71.22) * mm, v(23.22, -70.08) * mm, v(23.5, -68.35) * mm]});
            skFitSpline(sketch, "E257", {"points": [v(23.5, -68.35) * mm, v(23.9, -65.9) * mm, v(24.16, -65.2) * mm, v(25.1, -63.87) * mm]});
            skFitSpline(sketch, "E258", {"points": [v(25.1, -63.87) * mm, v(26.18, -62.33) * mm, v(26.35, -61.85) * mm, v(26.67, -59.46) * mm]});
            skFitSpline(sketch, "E259", {"points": [v(26.67, -59.46) * mm, v(26.98, -57.13) * mm, v(27.93, -54.18) * mm, v(28.89, -52.58) * mm]});
            skFitSpline(sketch, "E260", {"points": [v(28.89, -52.58) * mm, v(29.3, -51.88) * mm, v(30.25, -50.69) * mm, v(31, -49.93) * mm]});
            skFitSpline(sketch, "E261", {"points": [v(31, -49.93) * mm, v(33.26, -47.61) * mm, v(35.36, -45.01) * mm, v(35.9, -43.88) * mm]});
            skFitSpline(sketch, "E262", {"points": [v(35.9, -43.88) * mm, v(36.17, -43.28) * mm, v(36.49, -42.11) * mm, v(36.6, -41.27) * mm]});
            skFitSpline(sketch, "E263", {"points": [v(36.6, -41.27) * mm, v(36.81, -39.5) * mm, v(37.06, -39.06) * mm, v(38.37, -38.07) * mm]});
            skFitSpline(sketch, "E264", {"points": [v(38.37, -38.07) * mm, v(39.26, -37.4) * mm, v(40.2, -36.1) * mm, v(40.2, -35.57) * mm]});
            skFitSpline(sketch, "E265", {"points": [v(40.2, -35.57) * mm, v(40.2, -35.45) * mm, v(39.98, -35.11) * mm, v(39.7, -34.83) * mm]});
            skFitSpline(sketch, "E266", {"points": [v(39.7, -34.83) * mm, v(38.98, -34.12) * mm, v(38.86, -33.18) * mm, v(39.13, -30.68) * mm]});
            skFitSpline(sketch, "E267", {"points": [v(39.13, -30.68) * mm, v(39.26, -29.5) * mm, v(39.36, -26.93) * mm, v(39.36, -24.95) * mm]});
            skFitSpline(sketch, "E268", {"points": [v(39.36, -24.95) * mm, v(39.36, -21.87) * mm, v(39.3, -21.22) * mm, v(38.94, -20.3) * mm]});
            skFitSpline(sketch, "E269", {"points": [v(38.94, -20.3) * mm, v(38.39, -18.9) * mm, v(38.4, -18.51) * mm, v(39.04, -18) * mm]});
            skFitSpline(sketch, "E270", {"points": [v(39.04, -18) * mm, v(39.45, -17.69) * mm, v(39.57, -17.4) * mm, v(39.57, -16.76) * mm]});
            skFitSpline(sketch, "E271", {"points": [v(39.57, -16.76) * mm, v(39.57, -16.2) * mm, v(39.7, -15.8) * mm, v(39.97, -15.56) * mm]});
            skFitSpline(sketch, "E272", {"points": [v(39.97, -15.56) * mm, v(40.59, -15) * mm, v(40.32, -14.37) * mm, v(39.46, -14.37) * mm]});
            skFitSpline(sketch, "E273", {"points": [v(39.46, -14.37) * mm, v(38.38, -14.37) * mm, v(37.67, -13.4) * mm, v(37.67, -11.9) * mm]});
            skFitSpline(sketch, "E274", {"points": [v(37.67, -11.9) * mm, v(37.67, -10.72) * mm, v(37.93, -9.95) * mm, v(38.44, -9.65) * mm]});
            skFitSpline(sketch, "E275", {"points": [v(38.44, -9.65) * mm, v(39.04, -9.3) * mm, v(38.7, -8.02) * mm, v(38, -8.02) * mm]});
            skFitSpline(sketch, "E276", {"points": [v(38, -8.02) * mm, v(37.74, -8.02) * mm, v(37, -7.64) * mm, v(36.34, -7.18) * mm]});
            skFitSpline(sketch, "E277", {"points": [v(36.34, -7.18) * mm, v(35.18, -6.34) * mm, v(34.43, -6.12) * mm, v(34.18, -6.54) * mm]});
            skFitSpline(sketch, "E278", {"points": [v(34.18, -6.54) * mm, v(34.1, -6.66) * mm, v(33.87, -6.75) * mm, v(33.65, -6.75) * mm]});
            skFitSpline(sketch, "E279", {"points": [v(33.65, -6.75) * mm, v(33.07, -6.75) * mm, v(30.08, -5.09) * mm, v(29.83, -4.63) * mm]});
            skFitSpline(sketch, "E280", {"points": [v(29.83, -4.63) * mm, v(29.5, -4) * mm, v(29.6, -2.89) * mm, v(30.04, -2.22) * mm]});
            skFitSpline(sketch, "E281", {"points": [v(30.04, -2.22) * mm, v(30.4, -1.66) * mm, v(30.41, -1.54) * mm, v(30.14, -1.01) * mm]});
            skFitSpline(sketch, "E282", {"points": [v(30.14, -1.01) * mm, v(29.71, -0.19) * mm, v(29.76, 0.38) * mm, v(30.37, 1.68) * mm]});
            skFitSpline(sketch, "E283", {"points": [v(30.37, 1.68) * mm, v(30.96, 2.95) * mm, v(31, 3.5) * mm, v(30.65, 4.7) * mm]});
            skFitSpline(sketch, "E284", {"points": [v(30.65, 4.7) * mm, v(30.44, 5.4) * mm, v(30.46, 5.58) * mm, v(30.78, 5.93) * mm]});
            skFitSpline(sketch, "E285", {"points": [v(30.78, 5.93) * mm, v(31.13, 6.33) * mm, v(31.13, 6.4) * mm, v(30.68, 7.79) * mm]});
            skFitSpline(sketch, "E286", {"points": [v(30.68, 7.79) * mm, v(30.01, 9.8) * mm, v(29.64, 10.47) * mm, v(28.1, 12.43) * mm]});
            skFitSpline(sketch, "E287", {"points": [v(28.1, 12.43) * mm, v(27.35, 13.37) * mm, v(26.61, 14.44) * mm, v(26.46, 14.8) * mm]});
            skFitSpline(sketch, "E288", {"points": [v(26.46, 14.8) * mm, v(26, 15.95) * mm, v(26.28, 17.5) * mm, v(27.26, 19.16) * mm]});
            skFitSpline(sketch, "E289", {"points": [v(27.26, 19.16) * mm, v(28.4, 21.1) * mm, v(28.53, 21.7) * mm, v(27.93, 22.5) * mm]});
            skFitSpline(sketch, "E290", {"points": [v(27.93, 22.5) * mm, v(27.4, 23.23) * mm, v(27.46, 23.77) * mm, v(28.28, 25.17) * mm]});
            skFitSpline(sketch, "E291", {"points": [v(28.28, 25.17) * mm, v(28.94, 26.3) * mm, v(29.89, 26.9) * mm, v(31.02, 26.9) * mm]});
            skFitSpline(sketch, "E292", {"points": [v(31.02, 26.9) * mm, v(31.6, 26.9) * mm, v(32.1, 27.06) * mm, v(32.48, 27.36) * mm]});
            skFitSpline(sketch, "E293", {"points": [v(32.48, 27.36) * mm, v(33, 27.78) * mm, v(33.05, 27.91) * mm, v(32.96, 28.95) * mm]});
            skFitSpline(sketch, "E294", {"points": [v(32.96, 28.95) * mm, v(32.91, 29.57) * mm, v(32.82, 30.13) * mm, v(32.76, 30.19) * mm]});
            skFitSpline(sketch, "E295", {"points": [v(32.76, 30.19) * mm, v(32.7, 30.25) * mm, v(32.3, 30.15) * mm, v(31.89, 29.97) * mm]});
            skFitSpline(sketch, "E296", {"points": [v(31.89, 29.97) * mm, v(31.46, 29.8) * mm, v(31.06, 29.65) * mm, v(30.98, 29.65) * mm]});
            skFitSpline(sketch, "E297", {"points": [v(30.98, 29.65) * mm, v(30.9, 29.65) * mm, v(30.9, 30.37) * mm, v(30.97, 31.24) * mm]});
            skFitSpline(sketch, "E298", {"points": [v(30.97, 31.24) * mm, v(31.1, 32.73) * mm, v(31.07, 32.83) * mm, v(30.68, 32.83) * mm]});
            skFitSpline(sketch, "E299", {"points": [v(30.68, 32.83) * mm, v(30.45, 32.83) * mm, v(30.26, 32.97) * mm, v(30.26, 33.15) * mm]});
            skFitSpline(sketch, "E300", {"points": [v(30.26, 33.15) * mm, v(30.26, 33.32) * mm, v(30.16, 33.46) * mm, v(30.05, 33.46) * mm]});
            skFitSpline(sketch, "E301", {"points": [v(30.05, 33.46) * mm, v(29.69, 33.46) * mm, v(29.82, 34.44) * mm, v(30.23, 34.81) * mm]});
            skFitSpline(sketch, "E302", {"points": [v(30.23, 34.81) * mm, v(30.44, 35) * mm, v(31.16, 35.28) * mm, v(31.83, 35.42) * mm]});
            skFitSpline(sketch, "E303", {"points": [v(31.83, 35.42) * mm, v(32.85, 35.63) * mm, v(33.13, 35.62) * mm, v(33.6, 35.36) * mm]});
            skFitSpline(sketch, "E304", {"points": [v(33.6, 35.36) * mm, v(34.37, 34.93) * mm, v(34.48, 34.05) * mm, v(33.82, 33.73) * mm]});
            skFitSpline(sketch, "E305", {"points": [v(33.82, 33.73) * mm, v(33.34, 33.51) * mm, v(33.35, 33.5) * mm, v(34.15, 33.16) * mm]});
            skFitSpline(sketch, "E306", {"points": [v(34.15, 33.16) * mm, v(34.9, 32.83) * mm, v(34.99, 32.83) * mm, v(35.36, 33.17) * mm]});
            skFitSpline(sketch, "E307", {"points": [v(35.36, 33.17) * mm, v(35.58, 33.37) * mm, v(35.76, 33.64) * mm, v(35.76, 33.77) * mm]});
            skFitSpline(sketch, "E308", {"points": [v(35.76, 33.77) * mm, v(35.76, 33.9) * mm, v(36.1, 34.7) * mm, v(36.5, 35.56) * mm]});
            skFitSpline(sketch, "E309", {"points": [v(36.5, 35.56) * mm, v(37.29, 37.18) * mm, v(37.3, 37.75) * mm, v(36.61, 38.12) * mm]});
            skFitSpline(sketch, "E310", {"points": [v(36.61, 38.12) * mm, v(36.14, 38.38) * mm, v(35.55, 38.19) * mm, v(35.55, 37.78) * mm]});
            skFitSpline(sketch, "E311", {"points": [v(35.55, 37.78) * mm, v(35.55, 36.66) * mm, v(30.79, 39.12) * mm, v(30.36, 40.45) * mm]});
            skFitSpline(sketch, "E312", {"points": [v(30.36, 40.45) * mm, v(30.3, 40.68) * mm, v(30.34, 41.05) * mm, v(30.47, 41.29) * mm]});
            skFitSpline(sketch, "E313", {"points": [v(30.47, 41.29) * mm, v(30.77, 41.86) * mm, v(31.55, 41.83) * mm, v(33.01, 41.2) * mm]});
            skFitSpline(sketch, "E314", {"points": [v(33.01, 41.2) * mm, v(34.25, 40.67) * mm, v(34.4, 40.66) * mm, v(34.2, 41.18) * mm]});
            skFitSpline(sketch, "E315", {"points": [v(34.2, 41.18) * mm, v(34.13, 41.4) * mm, v(33.81, 41.5) * mm, v(33.34, 41.5) * mm]});
            skFitSpline(sketch, "E316", {"points": [v(33.34, 41.5) * mm, v(32.48, 41.5) * mm, v(32.37, 41.83) * mm, v(32.97, 42.57) * mm]});
            skFitSpline(sketch, "E317", {"points": [v(32.97, 42.57) * mm, v(33.3, 42.96) * mm, v(33.56, 43.04) * mm, v(34.54, 43.04) * mm]});
            skFitSpline(sketch, "E318", {"points": [v(34.54, 43.04) * mm, v(36.05, 43.02) * mm, v(36.12, 43.25) * mm, v(35.4, 45.67) * mm]});
            skFitSpline(sketch, "E319", {"points": [v(35.4, 45.67) * mm, v(34.98, 47.1) * mm, v(34.9, 47.7) * mm, v(35.01, 48.62) * mm]});
            skFitSpline(sketch, "E320", {"points": [v(35.01, 48.62) * mm, v(35.1, 49.37) * mm, v(35.26, 49.76) * mm, v(35.45, 49.76) * mm]});
            skFitSpline(sketch, "E321", {"points": [v(35.45, 49.76) * mm, v(35.79, 49.76) * mm, v(36.46, 48.04) * mm, v(36.81, 46.27) * mm]});
            skFitSpline(sketch, "E322", {"points": [v(36.81, 46.27) * mm, v(37.15, 44.53) * mm, v(37.45, 43.62) * mm, v(37.68, 43.62) * mm]});
            skFitSpline(sketch, "E323", {"points": [v(37.68, 43.62) * mm, v(37.8, 43.62) * mm, v(37.88, 43.84) * mm, v(37.88, 44.1) * mm]});
            skFitSpline(sketch, "E324", {"points": [v(37.88, 44.1) * mm, v(37.88, 44.74) * mm, v(36.88, 48.83) * mm, v(36.6, 49.36) * mm]});
            skFitSpline(sketch, "E325", {"points": [v(36.6, 49.36) * mm, v(36.47, 49.6) * mm, v(36.29, 50.3) * mm, v(36.19, 50.92) * mm]});
            skFitSpline(sketch, "E326", {"points": [v(36.19, 50.92) * mm, v(36.09, 51.54) * mm, v(35.8, 52.48) * mm, v(35.57, 53.01) * mm]});
            skFitSpline(sketch, "E327", {"points": [v(35.57, 53.01) * mm, v(35.31, 53.57) * mm, v(35.13, 54.41) * mm, v(35.13, 55.03) * mm]});
            skFitSpline(sketch, "E328", {"points": [v(35.13, 55.03) * mm, v(35.13, 56.37) * mm, v(34.52, 57.14) * mm, v(33.05, 57.66) * mm]});
            skFitSpline(sketch, "E329", {"points": [v(33.05, 57.66) * mm, v(31.97, 58.05) * mm, v(31.44, 58.5) * mm, v(31.02, 59.34) * mm]});
            skFitSpline(sketch, "E330", {"points": [v(31.02, 59.34) * mm, v(30.64, 60.08) * mm, v(29.4, 60.31) * mm, v(25.6, 60.34) * mm]});
            skFitSpline(sketch, "E331", {"points": [v(25.6, 60.34) * mm, v(21.36, 60.37) * mm, v(20.2, 60.66) * mm, v(19.62, 61.83) * mm]});
            skFitSpline(sketch, "E332", {"points": [v(19.62, 61.83) * mm, v(19.42, 62.24) * mm, v(19.25, 63.05) * mm, v(19.25, 63.63) * mm]});
            skFitSpline(sketch, "E333", {"points": [v(19.25, 63.63) * mm, v(19.24, 64.97) * mm, v(18.71, 66.14) * mm, v(17.39, 67.73) * mm]});
            skFitSpline(sketch, "E334", {"points": [v(17.39, 67.73) * mm, v(15.95, 69.45) * mm, v(15.56, 70.55) * mm, v(15.72, 72.4) * mm]});
            skFitSpline(sketch, "E335", {"points": [v(15.72, 72.4) * mm, v(15.89, 74.42) * mm, v(15.61, 75.26) * mm, v(14.57, 75.97) * mm]});
            skFitSpline(sketch, "E336", {"points": [v(14.57, 75.97) * mm, v(13.8, 76.48) * mm, v(12.94, 77.13) * mm, v(10.52, 78.96) * mm]});
            skFitSpline(sketch, "E337", {"points": [v(10.52, 78.96) * mm, v(9.93, 79.4) * mm, v(9.37, 79.6) * mm, v(8.4, 79.72) * mm]});
            skFitSpline(sketch, "E338", {"points": [v(8.4, 79.72) * mm, v(7.67, 79.8) * mm, v(6.83, 80.05) * mm, v(6.52, 80.27) * mm]});
            skFitSpline(sketch, "E339", {"points": [v(6.52, 80.27) * mm, v(5.73, 80.83) * mm, v(4.99, 80.76) * mm, v(4.18, 80.06) * mm]});
            skFitSpline(sketch, "E340", {"points": [v(4.18, 80.06) * mm, v(3.06, 79.09) * mm, v(2.62, 78.93) * mm, v(1.4, 79.08) * mm]});
            skFitSpline(sketch, "E341", {"points": [v(-1.23, 77.67) * mm, v(-2.35, 76.53) * mm, v(-2.88, 75.8) * mm, v(-3.2, 74.95) * mm]});
            skFitSpline(sketch, "E342", {"points": [v(-3.2, 74.95) * mm, v(-3.44, 74.31) * mm, v(-3.84, 73.58) * mm, v(-4.08, 73.32) * mm]});
            skFitSpline(sketch, "E343", {"points": [v(-4.08, 73.32) * mm, v(-4.6, 72.75) * mm, v(-5.86, 72.28) * mm, v(-7.31, 72.1) * mm]});
            skFitSpline(sketch, "E344", {"points": [v(-7.31, 72.1) * mm, v(-8.5, 71.94) * mm, v(-9.16, 71.58) * mm, v(-9.92, 70.68) * mm]});
            skFitSpline(sketch, "E345", {"points": [v(-9.92, 70.68) * mm, v(-10.62, 69.85) * mm, v(-11.46, 69.45) * mm, v(-12.51, 69.45) * mm]});
            skFitSpline(sketch, "E346", {"points": [v(-13.27, 67.07) * mm, v(-13.12, 64.4) * mm, v(-13.35, 63.34) * mm, v(-14.15, 63) * mm]});
            skFitSpline(sketch, "E347", {"points": [v(-14.15, 63) * mm, v(-14.41, 62.88) * mm, v(-14.68, 62.54) * mm, v(-14.74, 62.25) * mm]});
            skFitSpline(sketch, "E348", {"points": [v(-14.74, 62.25) * mm, v(-14.95, 61.27) * mm, v(-15.22, 60.8) * mm, v(-15.67, 60.66) * mm]});
            skFitSpline(sketch, "E349", {"points": [v(-15.67, 60.66) * mm, v(-16.3, 60.47) * mm, v(-17.15, 61.07) * mm, v(-17.15, 61.71) * mm]});
            skFitSpline(sketch, "E350", {"points": [v(-17.15, 61.71) * mm, v(-17.15, 62.4) * mm, v(-17.57, 62.62) * mm, v(-17.95, 62.12) * mm]});
            skFitSpline(sketch, "E351", {"points": [v(-17.95, 62.12) * mm, v(-18.25, 61.72) * mm, v(-18.24, 60.86) * mm, v(-17.87, 57.55) * mm]});
            skFitSpline(sketch, "E352", {"points": [v(-17.87, 57.55) * mm, v(-17.76, 56.53) * mm, v(-17.83, 56.11) * mm, v(-18.31, 54.9) * mm]});
            skFitSpline(sketch, "E353", {"points": [v(-18.43, 53.1) * mm, v(-18.09, 52.84) * mm, v(-18, 52.61) * mm, v(-18.12, 52.26) * mm]});
            skFitSpline(sketch, "E354", {"points": [v(-18.12, 52.26) * mm, v(-18.35, 51.5) * mm, v(-18.6, 51.29) * mm, v(-19.44, 51.14) * mm]});
            skFitSpline(sketch, "E355", {"points": [v(-19.44, 51.14) * mm, v(-20.16, 51.02) * mm, v(-20.25, 50.92) * mm, v(-20.59, 49.92) * mm]});
            skFitSpline(sketch, "E356", {"points": [v(-20.59, 49.92) * mm, v(-21.07, 48.49) * mm, v(-20.79, 47.82) * mm, v(-19.64, 47.63) * mm]});
            skFitSpline(sketch, "E357", {"points": [v(-19.64, 47.63) * mm, v(-18.7, 47.48) * mm, v(-18.1, 46.98) * mm, v(-17.9, 46.22) * mm]});
            skFitSpline(sketch, "E358", {"points": [v(-17.9, 46.22) * mm, v(-17.82, 45.92) * mm, v(-17.92, 44.77) * mm, v(-18.12, 43.68) * mm]});
            skFitSpline(sketch, "E359", {"points": [v(-18.12, 43.68) * mm, v(-18.44, 41.9) * mm, v(-18.54, 41.66) * mm, v(-19.03, 41.44) * mm]});
            skFitSpline(sketch, "E360", {"points": [v(-19.03, 41.44) * mm, v(-19.33, 41.3) * mm, v(-19.75, 41.02) * mm, v(-19.96, 40.82) * mm]});
            skFitSpline(sketch, "E361", {"points": [v(-19.96, 40.82) * mm, v(-20.16, 40.62) * mm, v(-20.6, 40.45) * mm, v(-20.94, 40.45) * mm]});
            skFitSpline(sketch, "E362", {"points": [v(-21.44, 41.8) * mm, v(-21.32, 43.27) * mm, v(-21.6, 44.43) * mm, v(-22.21, 44.98) * mm]});
            skFitSpline(sketch, "E363", {"points": [v(-22.21, 44.98) * mm, v(-22.54, 45.28) * mm, v(-22.7, 45.3) * mm, v(-23.16, 45.08) * mm]});
            skFitSpline(sketch, "E364", {"points": [v(-23.16, 45.08) * mm, v(-23.48, 44.93) * mm, v(-23.72, 44.65) * mm, v(-23.72, 44.41) * mm]});
            skFitSpline(sketch, "E365", {"points": [v(-23.72, 44.41) * mm, v(-23.72, 44.19) * mm, v(-24.06, 43.69) * mm, v(-24.47, 43.3) * mm]});
            skFitSpline(sketch, "E366", {"points": [v(-24.8, 41.05) * mm, v(-24.28, 39.2) * mm, v(-24.4, 38.43) * mm, v(-25.38, 37) * mm]});
            skFitSpline(sketch, "E367", {"points": [v(-25.38, 37) * mm, v(-26.38, 35.55) * mm, v(-26.52, 35.03) * mm, v(-26.15, 34.3) * mm]});
            skFitSpline(sketch, "E368", {"points": [v(-26.15, 34.3) * mm, v(-25.74, 33.52) * mm, v(-25.75, 32.64) * mm, v(-26.17, 31.34) * mm]});
            skFitSpline(sketch, "E369", {"points": [v(-26.17, 31.34) * mm, v(-26.5, 30.34) * mm, v(-26.5, 30.27) * mm, v(-26.05, 29.35) * mm]});
            skFitSpline(sketch, "E370", {"points": [v(-26.05, 29.35) * mm, v(-25.45, 28.12) * mm, v(-24.64, 27.64) * mm, v(-22.5, 27.27) * mm]});
            skFitSpline(sketch, "E371", {"points": [v(-22.5, 27.27) * mm, v(-21.03, 27.01) * mm, v(-20.71, 27.01) * mm, v(-20.51, 27.25) * mm]});
            skFitSpline(sketch, "E372", {"points": [v(-20.51, 27.25) * mm, v(-20.2, 27.62) * mm, v(-19.6, 27.62) * mm, v(-19.29, 27.24) * mm]});
            skFitSpline(sketch, "E373", {"points": [v(-19.29, 27.24) * mm, v(-18.74, 26.58) * mm, v(-18.77, 25.45) * mm, v(-19.37, 23.93) * mm]});
            skFitSpline(sketch, "E374", {"points": [v(-19.37, 23.93) * mm, v(-19.7, 23.08) * mm, v(-20.07, 22.46) * mm, v(-20.24, 22.46) * mm]});
            skFitSpline(sketch, "E375", {"points": [v(-20.24, 22.46) * mm, v(-20.4, 22.46) * mm, v(-20.54, 22.54) * mm, v(-20.54, 22.65) * mm]});
            skFitSpline(sketch, "E376", {"points": [v(-20.54, 22.65) * mm, v(-20.54, 23.08) * mm, v(-22.27, 25) * mm, v(-22.65, 25) * mm]});
            skFitSpline(sketch, "E377", {"points": [v(-22.65, 25) * mm, v(-23.23, 25) * mm, v(-23.72, 24.2) * mm, v(-23.72, 23.22) * mm]});
            skFitSpline(sketch, "E378", {"points": [v(-23.72, 23.22) * mm, v(-23.72, 22.72) * mm, v(-23.92, 22.04) * mm, v(-24.24, 21.5) * mm]});
            skFitSpline(sketch, "E379", {"points": [v(-24.24, 21.5) * mm, v(-24.66, 20.79) * mm, v(-24.75, 20.34) * mm, v(-24.74, 19.26) * mm]});
            skFitSpline(sketch, "E380", {"points": [v(-24.74, 19.26) * mm, v(-24.72, 18.51) * mm, v(-24.78, 17.69) * mm, v(-24.86, 17.43) * mm]});
            skFitSpline(sketch, "E381", {"points": [v(-24.86, 17.43) * mm, v(-25.08, 16.75) * mm, v(-24.82, 16.1) * mm, v(-24.33, 16.1) * mm]});
            skFitSpline(sketch, "E382", {"points": [v(-24.33, 16.1) * mm, v(-23.36, 16.1) * mm, v(-23.83, 14.55) * mm, v(-24.88, 14.3) * mm]});
            skFitSpline(sketch, "E383", {"points": [v(-24.88, 14.3) * mm, v(-25.3, 14.18) * mm, v(-25.36, 14.09) * mm, v(-25.2, 13.77) * mm]});
            skFitSpline(sketch, "E384", {"points": [v(-25.2, 13.77) * mm, v(-24.96, 13.34) * mm, v(-24.91, 12.23) * mm, v(-25.11, 12.03) * mm]});
            skFitSpline(sketch, "E385", {"points": [v(-25.11, 12.03) * mm, v(-25.18, 11.96) * mm, v(-25.46, 11.98) * mm, v(-25.73, 12.09) * mm]});
            skFitSpline(sketch, "E386", {"points": [v(-25.73, 12.09) * mm, v(-26.03, 12.2) * mm, v(-26.5, 12.18) * mm, v(-26.98, 12.04) * mm]});
            skFitSpline(sketch, "E387", {"points": [v(-26.98, 12.04) * mm, v(-28.78, 11.48) * mm, v(-28.79, 13.48) * mm, v(-26.99, 14.98) * mm]});
            skFitSpline(sketch, "E388", {"points": [v(-26.99, 14.98) * mm, v(-26.47, 15.42) * mm, v(-26.04, 15.92) * mm, v(-26.04, 16.09) * mm]});
            skFitSpline(sketch, "E389", {"points": [v(-26.04, 16.09) * mm, v(-26.04, 16.33) * mm, v(-26.1, 16.35) * mm, v(-26.3, 16.15) * mm]});
            skFitSpline(sketch, "E390", {"points": [v(-26.3, 16.15) * mm, v(-26.76, 15.69) * mm, v(-27.73, 15.86) * mm, v(-28.39, 16.52) * mm]});
            skFitSpline(sketch, "E391", {"points": [v(-28.39, 16.52) * mm, v(-28.98, 17.1) * mm, v(-29, 17.22) * mm, v(-29, 18.97) * mm]});
            skFitSpline(sketch, "E392", {"points": [v(-29, 18.97) * mm, v(-29, 20.63) * mm, v(-29.05, 20.82) * mm, v(-29.43, 20.91) * mm]});
            skFitSpline(sketch, "E393", {"points": [v(-29.43, 20.91) * mm, v(-30.19, 21.11) * mm, v(-29.94, 22.23) * mm, v(-28.69, 24.26) * mm]});
            skFitSpline(sketch, "E394", {"points": [v(-28.69, 24.26) * mm, v(-27.87, 25.58) * mm, v(-28, 27.33) * mm, v(-28.9, 27.33) * mm]});
            skFitSpline(sketch, "E395", {"points": [v(-28.9, 27.33) * mm, v(-29.17, 27.33) * mm, v(-29.7, 27.61) * mm, v(-30.07, 27.96) * mm]});
            skFitSpline(sketch, "E396", {"points": [v(-30.07, 27.96) * mm, v(-30.87, 28.71) * mm, v(-31.12, 28.76) * mm, v(-31.12, 28.14) * mm]});
            skFitSpline(sketch, "E397", {"points": [v(-31.12, 28.14) * mm, v(-31.12, 27.9) * mm, v(-30.7, 27.23) * mm, v(-30.17, 26.67) * mm]});
            skFitSpline(sketch, "E398", {"points": [v(-30.17, 26.67) * mm, v(-29.12, 25.55) * mm, v(-29.07, 25.4) * mm, v(-29.55, 24.9) * mm]});
            skFitSpline(sketch, "E399", {"points": [v(-29.55, 24.9) * mm, v(-30.1, 24.36) * mm, v(-30.96, 24.5) * mm, v(-31.6, 25.23) * mm]});
            skFitSpline(sketch, "E400", {"points": [v(-31.6, 25.23) * mm, v(-32.15, 25.85) * mm, v(-32.25, 25.88) * mm, v(-33.19, 25.74) * mm]});
            skFitSpline(sketch, "E401", {"points": [v(-33.19, 25.74) * mm, v(-34.37, 25.57) * mm, v(-35.26, 25.15) * mm, v(-35.43, 24.68) * mm]});
            skFitSpline(sketch, "E402", {"points": [v(-35.43, 24.68) * mm, v(-35.6, 24.23) * mm, v(-35.14, 24.08) * mm, v(-34.43, 24.35) * mm]});
            skFitSpline(sketch, "E403", {"points": [v(-34.43, 24.35) * mm, v(-34.1, 24.48) * mm, v(-33.54, 24.57) * mm, v(-33.15, 24.57) * mm]});
            skFitSpline(sketch, "E404", {"points": [v(-33.15, 24.57) * mm, v(-32.54, 24.57) * mm, v(-32.46, 24.5) * mm, v(-32.44, 24) * mm]});
            skFitSpline(sketch, "E405", {"points": [v(-32.44, 24) * mm, v(-32.43, 23.67) * mm, v(-32.27, 23.06) * mm, v(-32.1, 22.62) * mm]});
            skFitSpline(sketch, "E406", {"points": [v(-32.1, 22.62) * mm, v(-31.58, 21.42) * mm, v(-31.67, 20.28) * mm, v(-32.4, 18.86) * mm]});
            skFitSpline(sketch, "E407", {"points": [v(-32.4, 18.86) * mm, v(-33.14, 17.4) * mm, v(-33.17, 17.05) * mm, v(-32.63, 16.75) * mm]});
            skFitSpline(sketch, "E408", {"points": [v(-32.63, 16.75) * mm, v(-32.1, 16.47) * mm, v(-31.55, 14.82) * mm, v(-31.55, 13.54) * mm]});
            skFitSpline(sketch, "E409", {"points": [v(-31.55, 13.54) * mm, v(-31.55, 12.77) * mm, v(-31.45, 12.46) * mm, v(-31.11, 12.23) * mm]});
            skFitSpline(sketch, "E410", {"points": [v(-31.11, 12.23) * mm, v(-30.88, 12.06) * mm, v(-30.63, 11.6) * mm, v(-30.56, 11.18) * mm]});
            skFitSpline(sketch, "E411", {"points": [v(-30.56, 11.18) * mm, v(-30.46, 10.56) * mm, v(-30.52, 10.4) * mm, v(-30.91, 10.18) * mm]});
            skFitSpline(sketch, "E412", {"points": [v(-30.91, 10.18) * mm, v(-31.53, 9.85) * mm, v(-32.75, 10.1) * mm, v(-33.03, 10.6) * mm]});
            skFitSpline(sketch, "E413", {"points": [v(-33.03, 10.6) * mm, v(-33.14, 10.82) * mm, v(-33.25, 11.41) * mm, v(-33.26, 11.91) * mm]});
            skFitSpline(sketch, "E414", {"points": [v(-33.26, 11.91) * mm, v(-33.27, 12.53) * mm, v(-33.55, 13.4) * mm, v(-34.16, 14.63) * mm]});
            skFitSpline(sketch, "E415", {"points": [v(-34.16, 14.63) * mm, v(-34.97, 16.28) * mm, v(-35.1, 16.43) * mm, v(-35.72, 16.5) * mm]});
            skFitSpline(sketch, "E416", {"points": [v(-35.72, 16.5) * mm, v(-36.31, 16.55) * mm, v(-36.58, 16.38) * mm, v(-37.73, 15.23) * mm]});
            skFitSpline(sketch, "E417", {"points": [v(-37.73, 15.23) * mm, v(-38.93, 14.04) * mm, v(-39.01, 13.9) * mm, v(-38.59, 13.83) * mm]});
            skFitSpline(sketch, "E418", {"points": [v(-38.59, 13.83) * mm, v(-38.17, 13.76) * mm, v(-38.1, 13.62) * mm, v(-38.11, 12.76) * mm]});
            skFitSpline(sketch, "E419", {"points": [v(-38.11, 12.76) * mm, v(-38.12, 12.21) * mm, v(-38.4, 10.97) * mm, v(-38.75, 9.98) * mm]});
            skFitSpline(sketch, "E420", {"points": [v(-38.75, 9.98) * mm, v(-39.51, 7.8) * mm, v(-39.52, 7.37) * mm, v(-38.83, 5.2) * mm]});
            skFitSpline(sketch, "E421", {"points": [v(-38.83, 5.2) * mm, v(-38.38, 3.8) * mm, v(-38.3, 3.15) * mm, v(-38.32, 1.4) * mm]});
            skFitSpline(sketch, "E422", {"points": [v(-38.32, 1.4) * mm, v(-38.34, 0.23) * mm, v(-38.26, -1.1) * mm, v(-38.13, -1.57) * mm]});
            skFitSpline(sketch, "E423", {"points": [v(-38.13, -1.57) * mm, v(-37.77, -2.92) * mm, v(-37.86, -6.07) * mm, v(-38.34, -8.88) * mm]});
            skFitSpline(sketch, "E424", {"points": [v(-38.34, -8.88) * mm, v(-38.63, -10.58) * mm, v(-38.76, -12.12) * mm, v(-38.71, -13.3) * mm]});
            skFitSpline(sketch, "E425", {"points": [v(-38.71, -13.3) * mm, v(-38.65, -14.92) * mm, v(-38.56, -15.24) * mm, v(-37.96, -16.18) * mm]});
            skFitSpline(sketch, "E426", {"points": [v(-37.41, -20.41) * mm, v(-37.55, -24.06) * mm, v(-37.43, -24.65) * mm, v(-36.22, -26.18) * mm]});
            skFitSpline(sketch, "E427", {"points": [v(-36.22, -26.18) * mm, v(-34.5, -28.36) * mm, v(-33.66, -30.2) * mm, v(-33.66, -31.8) * mm]});
            skFitSpline(sketch, "E428", {"points": [v(-33.66, -31.8) * mm, v(-33.66, -32.5) * mm, v(-33.82, -32.8) * mm, v(-34.62, -33.66) * mm]});
            skFitSpline(sketch, "E429", {"points": [v(-34.62, -33.66) * mm, v(-35.46, -34.56) * mm, v(-35.57, -34.79) * mm, v(-35.57, -35.64) * mm]});
            skFitSpline(sketch, "E430", {"points": [v(-35.57, -35.64) * mm, v(-35.57, -36.85) * mm, v(-35.16, -37.86) * mm, v(-34.2, -38.96) * mm]});
            skFitSpline(sketch, "E431", {"points": [v(-34.2, -38.96) * mm, v(-33.8, -39.44) * mm, v(-33.28, -40.4) * mm, v(-33.04, -41.1) * mm]});
            skFitSpline(sketch, "E432", {"points": [v(-33.04, -41.1) * mm, v(-32.76, -41.93) * mm, v(-32.24, -42.8) * mm, v(-31.56, -43.59) * mm]});
            skFitSpline(sketch, "E433", {"points": [v(-31.56, -43.59) * mm, v(-29.64, -45.8) * mm, v(-29.61, -45.88) * mm, v(-29.6, -49.55) * mm]});
            skFitSpline(sketch, "E434", {"points": [v(-29.6, -49.55) * mm, v(-29.59, -51.33) * mm, v(-29.65, -53.1) * mm, v(-29.74, -53.47) * mm]});
            skFitSpline(sketch, "E435", {"points": [v(-29.74, -53.47) * mm, v(-29.87, -54.05) * mm, v(-29.78, -54.34) * mm, v(-29.2, -55.24) * mm]});
            skFitSpline(sketch, "E436", {"points": [v(-29.2, -55.24) * mm, v(-28.02, -57.1) * mm, v(-28.34, -58.63) * mm, v(-30.4, -60.92) * mm]});
            skFitSpline(sketch, "E437", {"points": [v(-30.9, -63.02) * mm, v(-30.62, -63.56) * mm, v(-29.54, -65.09) * mm, v(-28.5, -66.4) * mm]});
            skFitSpline(sketch, "E438", {"points": [v(-28.5, -66.4) * mm, v(-27.47, -67.73) * mm, v(-25.87, -70.02) * mm, v(-24.93, -71.5) * mm]});
            skFitSpline(sketch, "E439", {"points": [v(-24.93, -71.5) * mm, v(-21.66, -76.64) * mm, v(-20.53, -77.82) * mm, v(-18.3, -78.38) * mm]});
            skFitSpline(sketch, "E440", {"points": [v(-18.3, -78.38) * mm, v(-17.5, -78.58) * mm, v(-15.88, -79.13) * mm, v(-14.72, -79.6) * mm]});
            skFitSpline(sketch, "E441", {"points": [v(-14.72, -79.6) * mm, v(-13.56, -80.07) * mm, v(-12.22, -80.53) * mm, v(-11.76, -80.63) * mm]});
            skFitSpline(sketch, "E442", {"points": [v(-11.76, -80.63) * mm, v(-10.67, -80.86) * mm, v(-8.14, -80.7) * mm, v(-6.84, -80.3) * mm]});
            skFitSpline(sketch, "E443", {"points": [v(-34.5, 19.17) * mm, v(-34.65, 19.34) * mm, v(-35.11, 19.55) * mm, v(-35.54, 19.62) * mm]});
            skFitSpline(sketch, "E444", {"points": [v(-35.54, 19.62) * mm, v(-35.99, 19.7) * mm, v(-36.79, 20.15) * mm, v(-37.44, 20.68) * mm]});
            skFitSpline(sketch, "E445", {"points": [v(-37.44, 20.68) * mm, v(-38.07, 21.2) * mm, v(-38.96, 21.72) * mm, v(-39.42, 21.86) * mm]});
            skFitSpline(sketch, "E446", {"points": [v(-39.42, 21.86) * mm, v(-39.89, 22) * mm, v(-40.41, 22.34) * mm, v(-40.6, 22.6) * mm]});
            skFitSpline(sketch, "E447", {"points": [v(-40.6, 22.6) * mm, v(-40.88, 23.06) * mm, v(-40.88, 23.2) * mm, v(-40.52, 24.1) * mm]});
            skFitSpline(sketch, "E448", {"points": [v(-40.52, 24.1) * mm, v(-39.98, 25.46) * mm, v(-39.97, 28.27) * mm, v(-40.5, 29.07) * mm]});
            skFitSpline(sketch, "E449", {"points": [v(-40.5, 29.07) * mm, v(-40.94, 29.76) * mm, v(-40.96, 30.33) * mm, v(-40.55, 31.12) * mm]});
            skFitSpline(sketch, "E450", {"points": [v(-40.55, 31.12) * mm, v(-40.35, 31.5) * mm, v(-40.29, 32) * mm, v(-40.37, 32.52) * mm]});
            skFitSpline(sketch, "E451", {"points": [v(-40.37, 32.52) * mm, v(-40.49, 33.2) * mm, v(-40.43, 33.39) * mm, v(-39.97, 33.76) * mm]});
            skFitSpline(sketch, "E452", {"points": [v(-39.97, 33.76) * mm, v(-39.45, 34.2) * mm, v(-38.12, 36.16) * mm, v(-37.84, 36.9) * mm]});
            skFitSpline(sketch, "E453", {"points": [v(-37.84, 36.9) * mm, v(-37.74, 37.17) * mm, v(-37.47, 37.27) * mm, v(-36.87, 37.27) * mm]});
            skFitSpline(sketch, "E454", {"points": [v(-36.87, 37.27) * mm, v(-36.4, 37.27) * mm, v(-35.93, 37.4) * mm, v(-35.78, 37.6) * mm]});
            skFitSpline(sketch, "E455", {"points": [v(-35.78, 37.6) * mm, v(-35.64, 37.77) * mm, v(-35.2, 37.9) * mm, v(-34.82, 37.9) * mm]});
            skFitSpline(sketch, "E456", {"points": [v(-34.82, 37.9) * mm, v(-34.13, 37.9) * mm, v(-34.12, 37.9) * mm, v(-34.23, 37.12) * mm]});
            skFitSpline(sketch, "E457", {"points": [v(-34.23, 37.12) * mm, v(-34.47, 35.46) * mm, v(-34.75, 34.75) * mm, v(-35.37, 34.23) * mm]});
            skFitSpline(sketch, "E458", {"points": [v(-35.37, 34.23) * mm, v(-35.99, 33.7) * mm, v(-36, 33.67) * mm, v(-35.67, 33.16) * mm]});
            skFitSpline(sketch, "E459", {"points": [v(-35.67, 33.16) * mm, v(-34.87, 31.95) * mm, v(-36.1, 31.14) * mm, v(-37.5, 31.95) * mm]});
            skFitSpline(sketch, "E460", {"points": [v(-37.5, 31.95) * mm, v(-37.94, 32.2) * mm, v(-38.35, 32.4) * mm, v(-38.4, 32.4) * mm]});
            skFitSpline(sketch, "E461", {"points": [v(-38.4, 32.4) * mm, v(-38.63, 32.4) * mm, v(-38.23, 31.65) * mm, v(-37.44, 30.52) * mm]});
            skFitSpline(sketch, "E462", {"points": [v(-37.44, 30.52) * mm, v(-36.44, 29.1) * mm, v(-36.35, 28.09) * mm, v(-37.16, 27.33) * mm]});
            skFitSpline(sketch, "E463", {"points": [v(-37.16, 27.33) * mm, v(-37.75, 26.77) * mm, v(-37.88, 25.84) * mm, v(-37.36, 25.84) * mm]});
            skFitSpline(sketch, "E464", {"points": [v(-37.36, 25.84) * mm, v(-37.12, 25.84) * mm, v(-37.08, 25.7) * mm, v(-37.18, 25.26) * mm]});
            skFitSpline(sketch, "E465", {"points": [v(-37.18, 25.26) * mm, v(-37.37, 24.47) * mm, v(-37.66, 23.94) * mm, v(-37.9, 23.94) * mm]});
            skFitSpline(sketch, "E466", {"points": [v(-37.9, 23.94) * mm, v(-38.25, 23.94) * mm, v(-38.13, 23.18) * mm, v(-37.73, 22.82) * mm]});
            skFitSpline(sketch, "E467", {"points": [v(-37.73, 22.82) * mm, v(-37.52, 22.63) * mm, v(-36.88, 22.27) * mm, v(-36.3, 22.02) * mm]});
            skFitSpline(sketch, "E468", {"points": [v(-36.3, 22.02) * mm, v(-33.61, 20.87) * mm, v(-33.45, 20.76) * mm, v(-33.45, 20.13) * mm]});
            skFitSpline(sketch, "E469", {"points": [v(-33.45, 20.13) * mm, v(-33.45, 18.94) * mm, v(-33.94, 18.5) * mm, v(-34.5, 19.17) * mm]});
            skFitSpline(sketch, "E470", {"points": [v(-33.88, 20.11) * mm, v(-33.88, 20.2) * mm, v(-34.7, 20.65) * mm, v(-35.7, 21.1) * mm]});
            skFitSpline(sketch, "E471", {"points": [v(-35.7, 21.1) * mm, v(-38.2, 22.21) * mm, v(-38.53, 22.5) * mm, v(-38.53, 23.53) * mm]});
            skFitSpline(sketch, "E472", {"points": [v(-38.53, 23.53) * mm, v(-38.53, 23.99) * mm, v(-38.45, 24.36) * mm, v(-38.35, 24.36) * mm]});
            skFitSpline(sketch, "E473", {"points": [v(-38.35, 24.36) * mm, v(-38.26, 24.36) * mm, v(-38.08, 24.58) * mm, v(-37.96, 24.84) * mm]});
            skFitSpline(sketch, "E474", {"points": [v(-37.96, 24.84) * mm, v(-37.8, 25.2) * mm, v(-37.81, 25.39) * mm, v(-38.03, 25.6) * mm]});
            skFitSpline(sketch, "E475", {"points": [v(-38.03, 25.6) * mm, v(-38.5, 26.03) * mm, v(-38.36, 26.84) * mm, v(-37.67, 27.63) * mm]});
            skFitSpline(sketch, "E476", {"points": [v(-37.67, 27.63) * mm, v(-36.9, 28.51) * mm, v(-36.94, 28.8) * mm, v(-38.14, 30.48) * mm]});
            skFitSpline(sketch, "E477", {"points": [v(-38.14, 30.48) * mm, v(-38.63, 31.17) * mm, v(-38.96, 31.87) * mm, v(-38.96, 32.23) * mm]});
            skFitSpline(sketch, "E478", {"points": [v(-38.96, 32.23) * mm, v(-38.96, 32.75) * mm, v(-38.87, 32.83) * mm, v(-38.36, 32.83) * mm]});
            skFitSpline(sketch, "E479", {"points": [v(-38.36, 32.83) * mm, v(-38.03, 32.83) * mm, v(-37.58, 32.69) * mm, v(-37.36, 32.52) * mm]});
            skFitSpline(sketch, "E480", {"points": [v(-37.36, 32.52) * mm, v(-36.98, 32.23) * mm, v(-36, 32.07) * mm, v(-36, 32.3) * mm]});
            skFitSpline(sketch, "E481", {"points": [v(-36, 32.3) * mm, v(-36, 32.35) * mm, v(-36.15, 32.73) * mm, v(-36.35, 33.14) * mm]});
            skFitSpline(sketch, "E482", {"points": [v(-35.92, 34.57) * mm, v(-35.27, 35.14) * mm, v(-35.1, 35.46) * mm, v(-34.96, 36.38) * mm]});
            skFitSpline(sketch, "E483", {"points": [v(-34.96, 36.38) * mm, v(-34.86, 36.99) * mm, v(-34.82, 37.49) * mm, v(-34.87, 37.49) * mm]});
            skFitSpline(sketch, "E484", {"points": [v(-34.87, 37.49) * mm, v(-34.91, 37.49) * mm, v(-35.23, 37.28) * mm, v(-35.56, 37.04) * mm]});
            skFitSpline(sketch, "E485", {"points": [v(-35.56, 37.04) * mm, v(-35.96, 36.74) * mm, v(-36.36, 36.62) * mm, v(-36.72, 36.69) * mm]});
            skFitSpline(sketch, "E486", {"points": [v(-36.72, 36.69) * mm, v(-37.02, 36.75) * mm, v(-37.26, 36.72) * mm, v(-37.26, 36.64) * mm]});
            skFitSpline(sketch, "E487", {"points": [v(-37.26, 36.64) * mm, v(-37.26, 36.35) * mm, v(-39.4, 33.25) * mm, v(-39.6, 33.25) * mm]});
            skFitSpline(sketch, "E488", {"points": [v(-39.6, 33.25) * mm, v(-39.71, 33.25) * mm, v(-39.8, 32.75) * mm, v(-39.8, 32.14) * mm]});
            skFitSpline(sketch, "E489", {"points": [v(-39.8, 32.14) * mm, v(-39.81, 31.5) * mm, v(-39.95, 30.86) * mm, v(-40.13, 30.62) * mm]});
            skFitSpline(sketch, "E490", {"points": [v(-40.13, 30.62) * mm, v(-40.4, 30.26) * mm, v(-40.4, 30.15) * mm, v(-40.08, 29.67) * mm]});
            skFitSpline(sketch, "E491", {"points": [v(-40.08, 29.67) * mm, v(-39.54, 28.86) * mm, v(-39.43, 25.58) * mm, v(-39.9, 24.18) * mm]});
            skFitSpline(sketch, "E492", {"points": [v(-39.9, 24.18) * mm, v(-40.1, 23.59) * mm, v(-40.2, 23.02) * mm, v(-40.14, 22.92) * mm]});
            skFitSpline(sketch, "E493", {"points": [v(-40.14, 22.92) * mm, v(-40.08, 22.82) * mm, v(-39.57, 22.56) * mm, v(-39.02, 22.35) * mm]});
            skFitSpline(sketch, "E494", {"points": [v(-39.02, 22.35) * mm, v(-38.46, 22.15) * mm, v(-37.5, 21.56) * mm, v(-36.87, 21.05) * mm]});
            skFitSpline(sketch, "E495", {"points": [v(-36.87, 21.05) * mm, v(-36.12, 20.45) * mm, v(-35.53, 20.13) * mm, v(-35.13, 20.13) * mm]});
            skFitSpline(sketch, "E496", {"points": [v(-35.13, 20.13) * mm, v(-34.8, 20.13) * mm, v(-34.48, 20.03) * mm, v(-34.4, 19.91) * mm]});
            skFitSpline(sketch, "E497", {"points": [v(-34.4, 19.91) * mm, v(-34.26, 19.68) * mm, v(-33.88, 19.83) * mm, v(-33.88, 20.11) * mm]});
            skFitSpline(sketch, "E498", {"points": [v(-35.84, 27.25) * mm, v(-35.9, 27.35) * mm, v(-36.01, 27.96) * mm, v(-36.1, 28.6) * mm]});
            skFitSpline(sketch, "E499", {"points": [v(-36.1, 28.6) * mm, v(-36.27, 30.1) * mm, v(-35.9, 30.72) * mm, v(-35.07, 30.34) * mm]});
            skFitSpline(sketch, "E500", {"points": [v(-35.07, 30.34) * mm, v(-34.7, 30.18) * mm, v(-34.56, 29.98) * mm, v(-34.64, 29.77) * mm]});
            skFitSpline(sketch, "E501", {"points": [v(-34.64, 29.77) * mm, v(-34.74, 29.52) * mm, v(-34.61, 29.44) * mm, v(-34.1, 29.44) * mm]});
            skFitSpline(sketch, "E502", {"points": [v(-34.1, 29.44) * mm, v(-33.14, 29.44) * mm, v(-32.6, 29.1) * mm, v(-32.6, 28.48) * mm]});
            skFitSpline(sketch, "E503", {"points": [v(-32.6, 28.48) * mm, v(-32.6, 28.2) * mm, v(-32.71, 27.96) * mm, v(-32.85, 27.96) * mm]});
            skFitSpline(sketch, "E504", {"points": [v(-32.85, 27.96) * mm, v(-32.98, 27.96) * mm, v(-33.2, 27.8) * mm, v(-33.34, 27.62) * mm]});
            skFitSpline(sketch, "E505", {"points": [v(-33.34, 27.62) * mm, v(-33.62, 27.24) * mm, v(-35.65, 26.94) * mm, v(-35.84, 27.25) * mm]});
            skFitSpline(sketch, "E506", {"points": [v(-33.88, 28.07) * mm, v(-33.88, 28.24) * mm, v(-33.73, 28.38) * mm, v(-33.56, 28.38) * mm]});
            skFitSpline(sketch, "E507", {"points": [v(-33.56, 28.38) * mm, v(-33.38, 28.38) * mm, v(-33.24, 28.48) * mm, v(-33.24, 28.6) * mm]});
            skFitSpline(sketch, "E508", {"points": [v(-33.24, 28.6) * mm, v(-33.24, 28.71) * mm, v(-33.73, 28.8) * mm, v(-34.32, 28.8) * mm]});
            skFitSpline(sketch, "E509", {"points": [v(-34.32, 28.8) * mm, v(-35.4, 28.8) * mm, v(-35.4, 28.81) * mm, v(-35.31, 29.43) * mm]});
            skFitSpline(sketch, "E510", {"points": [v(-35.31, 29.43) * mm, v(-35.26, 29.77) * mm, v(-35.3, 30) * mm, v(-35.4, 29.95) * mm]});
            skFitSpline(sketch, "E511", {"points": [v(-35.4, 29.95) * mm, v(-35.6, 29.82) * mm, v(-35.62, 28.91) * mm, v(-35.44, 28.23) * mm]});
            skFitSpline(sketch, "E512", {"points": [v(-35.44, 28.23) * mm, v(-35.33, 27.85) * mm, v(-35.16, 27.75) * mm, v(-34.6, 27.75) * mm]});
            skFitSpline(sketch, "E513", {"points": [v(-34.6, 27.75) * mm, v(-34.1, 27.75) * mm, v(-33.88, 27.85) * mm, v(-33.88, 28.07) * mm]});
            skFitSpline(sketch, "E514", {"points": [v(-34.5, 30.49) * mm, v(-34.87, 31.18) * mm, v(-34.75, 31.97) * mm, v(-34.2, 32.53) * mm]});
            skFitSpline(sketch, "E515", {"points": [v(-34.2, 32.53) * mm, v(-33.9, 32.82) * mm, v(-33.66, 33.2) * mm, v(-33.66, 33.37) * mm]});
            skFitSpline(sketch, "E516", {"points": [v(-33.66, 33.37) * mm, v(-33.66, 33.54) * mm, v(-33.57, 33.68) * mm, v(-33.45, 33.68) * mm]});
            skFitSpline(sketch, "E517", {"points": [v(-33.45, 33.68) * mm, v(-33.34, 33.68) * mm, v(-33.24, 33.6) * mm, v(-33.24, 33.51) * mm]});
            skFitSpline(sketch, "E518", {"points": [v(-33.24, 33.51) * mm, v(-33.24, 33.42) * mm, v(-32.95, 33.24) * mm, v(-32.6, 33.1) * mm]});
            skFitSpline(sketch, "E519", {"points": [v(-32.6, 33.1) * mm, v(-31.72, 32.77) * mm, v(-31.8, 32.27) * mm, v(-32.94, 31.08) * mm]});
            skFitSpline(sketch, "E520", {"points": [v(-32.94, 31.08) * mm, v(-34, 29.96) * mm, v(-34.19, 29.9) * mm, v(-34.5, 30.49) * mm]});
            skFitSpline(sketch, "E521", {"points": [v(-32.6, 32.45) * mm, v(-32.6, 32.54) * mm, v(-32.75, 32.62) * mm, v(-32.92, 32.62) * mm]});
            skFitSpline(sketch, "E522", {"points": [v(-32.92, 32.62) * mm, v(-33.1, 32.62) * mm, v(-33.24, 32.53) * mm, v(-33.24, 32.43) * mm]});
            skFitSpline(sketch, "E523", {"points": [v(-33.24, 32.43) * mm, v(-33.24, 32.33) * mm, v(-33.43, 32.2) * mm, v(-33.66, 32.13) * mm]});
            skFitSpline(sketch, "E524", {"points": [v(-33.66, 32.13) * mm, v(-33.96, 32.06) * mm, v(-34.09, 31.84) * mm, v(-34.09, 31.43) * mm]});
            skFitSpline(sketch, "E525", {"points": [v(-33.35, 31.56) * mm, v(-32.94, 31.95) * mm, v(-32.6, 32.35) * mm, v(-32.6, 32.45) * mm]});
            skSolve(sketch);
        }
        {
            var Q0;
            Q0=makeQuery(id+"F0.imprint","IMPRINT",FACE,{"disambiguationData":[TD([[makeQuery(id+"F0.imprint","IMPRINT",EDGE,{"derivedFrom":sQuery(id+"F0.wireOp",EDGE,"E12")}),1.0]])]});
            var Q1;
            Q1=makeQuery(id+"F0.imprint","IMPRINT",FACE,{"disambiguationData":[TD([[makeQuery(id+"F0.imprint","IMPRINT",EDGE,{"derivedFrom":sQuery(id+"F0.wireOp",EDGE,"E26")}),1.0]])]});
            var Q2;
            Q2=makeQuery(id+"F0.imprint","IMPRINT",FACE,{"disambiguationData":[TD([[makeQuery(id+"F0.imprint","IMPRINT",EDGE,{"derivedFrom":sQuery(id+"F0.wireOp",EDGE,"E506")}),1.0]])]});
            var Q3;
            Q3=makeQuery(id+"F0.imprint","IMPRINT",FACE,{"disambiguationData":[TD([[makeQuery(id+"F0.imprint","IMPRINT",EDGE,{"derivedFrom":sQuery(id+"F0.wireOp",EDGE,"E28")}),1.0]])]});
            extrude(context, id + "F1", {"entities" : qUnion([Q0, Q1, Q2, Q3]), "depth" : 3 * mm, "offsetDistance" : 25 * mm});
        }
        {
            var Q0;
            Q0=makeQuery(id+"F1.opExtrude","CAP_FACE",FACE,{"disambiguationData":[OSD([sQuery(id+"F0.wireOp",EDGE,"E12"),sQuery(id+"F0.wireOp",EDGE,"E13"),sQuery(id+"F0.wireOp",EDGE,"E14"),sQuery(id+"F0.wireOp",EDGE,"E15"),sQuery(id+"F0.wireOp",EDGE,"E16"),sQuery(id+"F0.wireOp",EDGE,"E17"),sQuery(id+"F0.wireOp",EDGE,"E18"),sQuery(id+"F0.wireOp",EDGE,"E19"),sQuery(id+"F0.wireOp",EDGE,"E20"),sQuery(id+"F0.wireOp",EDGE,"E21"),sQuery(id+"F0.wireOp",EDGE,"E22"),sQuery(id+"F0.wireOp",EDGE,"E23"),sQuery(id+"F0.wireOp",EDGE,"E24"),sQuery(id+"F0.wireOp",EDGE,"E25"),sQuery(id+"F0.wireOp",EDGE,"E233"),sQuery(id+"F0.wireOp",EDGE,"E234"),sQuery(id+"F0.wireOp",EDGE,"E235"),sQuery(id+"F0.wireOp",EDGE,"E236"),sQuery(id+"F0.wireOp",EDGE,"E237"),sQuery(id+"F0.wireOp",EDGE,"E238"),sQuery(id+"F0.wireOp",EDGE,"E239"),sQuery(id+"F0.wireOp",EDGE,"E240"),sQuery(id+"F0.wireOp",EDGE,"E241"),sQuery(id+"F0.wireOp",EDGE,"E242"),sQuery(id+"F0.wireOp",EDGE,"E243"),sQuery(id+"F0.wireOp",EDGE,"E244"),sQuery(id+"F0.wireOp",EDGE,"E245"),sQuery(id+"F0.wireOp",EDGE,"E246"),sQuery(id+"F0.wireOp",EDGE,"E247"),sQuery(id+"F0.wireOp",EDGE,"E248"),sQuery(id+"F0.wireOp",EDGE,"E249"),sQuery(id+"F0.wireOp",EDGE,"E250"),sQuery(id+"F0.wireOp",EDGE,"E251"),sQuery(id+"F0.wireOp",EDGE,"E252"),sQuery(id+"F0.wireOp",EDGE,"E253"),sQuery(id+"F0.wireOp",EDGE,"E254"),sQuery(id+"F0.wireOp",EDGE,"E255"),sQuery(id+"F0.wireOp",EDGE,"E256"),sQuery(id+"F0.wireOp",EDGE,"E257"),sQuery(id+"F0.wireOp",EDGE,"E258"),sQuery(id+"F0.wireOp",EDGE,"E259"),sQuery(id+"F0.wireOp",EDGE,"E260"),sQuery(id+"F0.wireOp",EDGE,"E261"),sQuery(id+"F0.wireOp",EDGE,"E262"),sQuery(id+"F0.wireOp",EDGE,"E263"),sQuery(id+"F0.wireOp",EDGE,"E264"),sQuery(id+"F0.wireOp",EDGE,"E265"),sQuery(id+"F0.wireOp",EDGE,"E266"),sQuery(id+"F0.wireOp",EDGE,"E267"),sQuery(id+"F0.wireOp",EDGE,"E268"),sQuery(id+"F0.wireOp",EDGE,"E269"),sQuery(id+"F0.wireOp",EDGE,"E270"),sQuery(id+"F0.wireOp",EDGE,"E271"),sQuery(id+"F0.wireOp",EDGE,"E272"),sQuery(id+"F0.wireOp",EDGE,"E273"),sQuery(id+"F0.wireOp",EDGE,"E274"),sQuery(id+"F0.wireOp",EDGE,"E275"),sQuery(id+"F0.wireOp",EDGE,"E276"),sQuery(id+"F0.wireOp",EDGE,"E277"),sQuery(id+"F0.wireOp",EDGE,"E278"),sQuery(id+"F0.wireOp",EDGE,"E279"),sQuery(id+"F0.wireOp",EDGE,"E280"),sQuery(id+"F0.wireOp",EDGE,"E281"),sQuery(id+"F0.wireOp",EDGE,"E282"),sQuery(id+"F0.wireOp",EDGE,"E283"),sQuery(id+"F0.wireOp",EDGE,"E284"),sQuery(id+"F0.wireOp",EDGE,"E285"),sQuery(id+"F0.wireOp",EDGE,"E286"),sQuery(id+"F0.wireOp",EDGE,"E287"),sQuery(id+"F0.wireOp",EDGE,"E288"),sQuery(id+"F0.wireOp",EDGE,"E289"),sQuery(id+"F0.wireOp",EDGE,"E290"),sQuery(id+"F0.wireOp",EDGE,"E291"),sQuery(id+"F0.wireOp",EDGE,"E292"),sQuery(id+"F0.wireOp",EDGE,"E293"),sQuery(id+"F0.wireOp",EDGE,"E294"),sQuery(id+"F0.wireOp",EDGE,"E295"),sQuery(id+"F0.wireOp",EDGE,"E296"),sQuery(id+"F0.wireOp",EDGE,"E297"),sQuery(id+"F0.wireOp",EDGE,"E298"),sQuery(id+"F0.wireOp",EDGE,"E299"),sQuery(id+"F0.wireOp",EDGE,"E300"),sQuery(id+"F0.wireOp",EDGE,"E301"),sQuery(id+"F0.wireOp",EDGE,"E302"),sQuery(id+"F0.wireOp",EDGE,"E303"),sQuery(id+"F0.wireOp",EDGE,"E304"),sQuery(id+"F0.wireOp",EDGE,"E305"),sQuery(id+"F0.wireOp",EDGE,"E306"),sQuery(id+"F0.wireOp",EDGE,"E307"),sQuery(id+"F0.wireOp",EDGE,"E308"),sQuery(id+"F0.wireOp",EDGE,"E309"),sQuery(id+"F0.wireOp",EDGE,"E310"),sQuery(id+"F0.wireOp",EDGE,"E311"),sQuery(id+"F0.wireOp",EDGE,"E312"),sQuery(id+"F0.wireOp",EDGE,"E313"),sQuery(id+"F0.wireOp",EDGE,"E314"),sQuery(id+"F0.wireOp",EDGE,"E315"),sQuery(id+"F0.wireOp",EDGE,"E316"),sQuery(id+"F0.wireOp",EDGE,"E317"),sQuery(id+"F0.wireOp",EDGE,"E318"),sQuery(id+"F0.wireOp",EDGE,"E319"),sQuery(id+"F0.wireOp",EDGE,"E320"),sQuery(id+"F0.wireOp",EDGE,"E321"),sQuery(id+"F0.wireOp",EDGE,"E322"),sQuery(id+"F0.wireOp",EDGE,"E323"),sQuery(id+"F0.wireOp",EDGE,"E324"),sQuery(id+"F0.wireOp",EDGE,"E325"),sQuery(id+"F0.wireOp",EDGE,"E326"),sQuery(id+"F0.wireOp",EDGE,"E327"),sQuery(id+"F0.wireOp",EDGE,"E328"),sQuery(id+"F0.wireOp",EDGE,"E329"),sQuery(id+"F0.wireOp",EDGE,"E330"),sQuery(id+"F0.wireOp",EDGE,"E331"),sQuery(id+"F0.wireOp",EDGE,"E332"),sQuery(id+"F0.wireOp",EDGE,"E333"),sQuery(id+"F0.wireOp",EDGE,"E334"),sQuery(id+"F0.wireOp",EDGE,"E335"),sQuery(id+"F0.wireOp",EDGE,"E336"),sQuery(id+"F0.wireOp",EDGE,"E337"),sQuery(id+"F0.wireOp",EDGE,"E338"),sQuery(id+"F0.wireOp",EDGE,"E339"),sQuery(id+"F0.wireOp",EDGE,"E340"),sQuery(id+"F0.wireOp",EDGE,"E341"),sQuery(id+"F0.wireOp",EDGE,"E342"),sQuery(id+"F0.wireOp",EDGE,"E343"),sQuery(id+"F0.wireOp",EDGE,"E344"),sQuery(id+"F0.wireOp",EDGE,"E345"),sQuery(id+"F0.wireOp",EDGE,"E346"),sQuery(id+"F0.wireOp",EDGE,"E347"),sQuery(id+"F0.wireOp",EDGE,"E348"),sQuery(id+"F0.wireOp",EDGE,"E349"),sQuery(id+"F0.wireOp",EDGE,"E350"),sQuery(id+"F0.wireOp",EDGE,"E351"),sQuery(id+"F0.wireOp",EDGE,"E352"),sQuery(id+"F0.wireOp",EDGE,"E353"),sQuery(id+"F0.wireOp",EDGE,"E354"),sQuery(id+"F0.wireOp",EDGE,"E355"),sQuery(id+"F0.wireOp",EDGE,"E356"),sQuery(id+"F0.wireOp",EDGE,"E357"),sQuery(id+"F0.wireOp",EDGE,"E358"),sQuery(id+"F0.wireOp",EDGE,"E359"),sQuery(id+"F0.wireOp",EDGE,"E360"),sQuery(id+"F0.wireOp",EDGE,"E361"),sQuery(id+"F0.wireOp",EDGE,"E362"),sQuery(id+"F0.wireOp",EDGE,"E363"),sQuery(id+"F0.wireOp",EDGE,"E364"),sQuery(id+"F0.wireOp",EDGE,"E365"),sQuery(id+"F0.wireOp",EDGE,"E366"),sQuery(id+"F0.wireOp",EDGE,"E367"),sQuery(id+"F0.wireOp",EDGE,"E368"),sQuery(id+"F0.wireOp",EDGE,"E369"),sQuery(id+"F0.wireOp",EDGE,"E370"),sQuery(id+"F0.wireOp",EDGE,"E371"),sQuery(id+"F0.wireOp",EDGE,"E372"),sQuery(id+"F0.wireOp",EDGE,"E373"),sQuery(id+"F0.wireOp",EDGE,"E374"),sQuery(id+"F0.wireOp",EDGE,"E375"),sQuery(id+"F0.wireOp",EDGE,"E376"),sQuery(id+"F0.wireOp",EDGE,"E377"),sQuery(id+"F0.wireOp",EDGE,"E378"),sQuery(id+"F0.wireOp",EDGE,"E379"),sQuery(id+"F0.wireOp",EDGE,"E380"),sQuery(id+"F0.wireOp",EDGE,"E381"),sQuery(id+"F0.wireOp",EDGE,"E382"),sQuery(id+"F0.wireOp",EDGE,"E383"),sQuery(id+"F0.wireOp",EDGE,"E384"),sQuery(id+"F0.wireOp",EDGE,"E385"),sQuery(id+"F0.wireOp",EDGE,"E386"),sQuery(id+"F0.wireOp",EDGE,"E387"),sQuery(id+"F0.wireOp",EDGE,"E388"),sQuery(id+"F0.wireOp",EDGE,"E389"),sQuery(id+"F0.wireOp",EDGE,"E390"),sQuery(id+"F0.wireOp",EDGE,"E391"),sQuery(id+"F0.wireOp",EDGE,"E392"),sQuery(id+"F0.wireOp",EDGE,"E393"),sQuery(id+"F0.wireOp",EDGE,"E394"),sQuery(id+"F0.wireOp",EDGE,"E395"),sQuery(id+"F0.wireOp",EDGE,"E396"),sQuery(id+"F0.wireOp",EDGE,"E397"),sQuery(id+"F0.wireOp",EDGE,"E398"),sQuery(id+"F0.wireOp",EDGE,"E399"),sQuery(id+"F0.wireOp",EDGE,"E400"),sQuery(id+"F0.wireOp",EDGE,"E401"),sQuery(id+"F0.wireOp",EDGE,"E402"),sQuery(id+"F0.wireOp",EDGE,"E403"),sQuery(id+"F0.wireOp",EDGE,"E404"),sQuery(id+"F0.wireOp",EDGE,"E405"),sQuery(id+"F0.wireOp",EDGE,"E406"),sQuery(id+"F0.wireOp",EDGE,"E407"),sQuery(id+"F0.wireOp",EDGE,"E408"),sQuery(id+"F0.wireOp",EDGE,"E409"),sQuery(id+"F0.wireOp",EDGE,"E410"),sQuery(id+"F0.wireOp",EDGE,"E411"),sQuery(id+"F0.wireOp",EDGE,"E412"),sQuery(id+"F0.wireOp",EDGE,"E413"),sQuery(id+"F0.wireOp",EDGE,"E414"),sQuery(id+"F0.wireOp",EDGE,"E415"),sQuery(id+"F0.wireOp",EDGE,"E416"),sQuery(id+"F0.wireOp",EDGE,"E417"),sQuery(id+"F0.wireOp",EDGE,"E418"),sQuery(id+"F0.wireOp",EDGE,"E419"),sQuery(id+"F0.wireOp",EDGE,"E420"),sQuery(id+"F0.wireOp",EDGE,"E421"),sQuery(id+"F0.wireOp",EDGE,"E422"),sQuery(id+"F0.wireOp",EDGE,"E423"),sQuery(id+"F0.wireOp",EDGE,"E424"),sQuery(id+"F0.wireOp",EDGE,"E425"),sQuery(id+"F0.wireOp",EDGE,"E426"),sQuery(id+"F0.wireOp",EDGE,"E427"),sQuery(id+"F0.wireOp",EDGE,"E428"),sQuery(id+"F0.wireOp",EDGE,"E429"),sQuery(id+"F0.wireOp",EDGE,"E430"),sQuery(id+"F0.wireOp",EDGE,"E431"),sQuery(id+"F0.wireOp",EDGE,"E432"),sQuery(id+"F0.wireOp",EDGE,"E433"),sQuery(id+"F0.wireOp",EDGE,"E434"),sQuery(id+"F0.wireOp",EDGE,"E435"),sQuery(id+"F0.wireOp",EDGE,"E436"),sQuery(id+"F0.wireOp",EDGE,"E437"),sQuery(id+"F0.wireOp",EDGE,"E438"),sQuery(id+"F0.wireOp",EDGE,"E439"),sQuery(id+"F0.wireOp",EDGE,"E440"),sQuery(id+"F0.wireOp",EDGE,"E441"),sQuery(id+"F0.wireOp",EDGE,"E442")])],"isStart":false});
            var sketch = newSketch(context, id + "F2", { "sketchPlane" : qUnion([Q0])});
            skLineSegment(sketch, "E526", {"start": v(-18.12, 52.26) * mm, "end": v(-2.72, 52.26) * mm});
            skLineSegment(sketch, "E527", {"start": v(-2.72, 52.26) * mm, "end": v(-2.72, 57.25) * mm});
            skLineSegment(sketch, "E528", {"start": v(-2.72, 57.25) * mm, "end": v(9.81, 57.25) * mm});
            skLineSegment(sketch, "E529", {"start": v(9.81, 57.25) * mm, "end": v(9.81, 54.32) * mm});
            skLineSegment(sketch, "E530", {"start": v(9.81, 54.32) * mm, "end": v(15.66, 54.32) * mm});
            skLineSegment(sketch, "E531", {"start": v(15.66, 54.32) * mm, "end": v(15.66, 46.72) * mm});
            skLineSegment(sketch, "E532", {"start": v(15.66, 46.72) * mm, "end": v(7.64, 37.18) * mm});
            skLineSegment(sketch, "E533", {"start": v(7.64, 37.18) * mm, "end": v(-2.52, 37.18) * mm});
            skLineSegment(sketch, "E534", {"start": v(-2.52, 37.18) * mm, "end": v(-2.52, 39.55) * mm});
            skLineSegment(sketch, "E535", {"start": v(-2.52, 39.55) * mm, "end": v(-24.5, 39.55) * mm});
            skLineSegment(sketch, "E536", {"start": v(15.66, 51.29) * mm, "end": v(21.38, 51.29) * mm});
            skLineSegment(sketch, "E537", {"start": v(21.38, 51.29) * mm, "end": v(21.38, 60.62) * mm});
            skLineSegment(sketch, "E538", {"start": v(7.64, 37.18) * mm, "end": v(7.64, 29.75) * mm});
            skLineSegment(sketch, "E539", {"start": v(7.64, 29.75) * mm, "end": v(12.1, 22.91) * mm});
            skLineSegment(sketch, "E540", {"start": v(12.1, 22.91) * mm, "end": v(27.69, 22.91) * mm});
            skLineSegment(sketch, "E541", {"start": v(12.1, 22.91) * mm, "end": v(12.1, 16.76) * mm});
            skLineSegment(sketch, "E542", {"start": v(12.1, 16.76) * mm, "end": v(1.97, 16.76) * mm});
            skLineSegment(sketch, "E543", {"start": v(1.97, 16.76) * mm, "end": v(-2.49, 11.93) * mm});
            skLineSegment(sketch, "E544", {"start": v(-2.49, 11.93) * mm, "end": v(-2.49, -5.73) * mm});
            skLineSegment(sketch, "E545", {"start": v(-2.49, -5.73) * mm, "end": v(-11.22, -5.73) * mm});
            skLineSegment(sketch, "E546", {"start": v(-11.22, -5.73) * mm, "end": v(-11.22, -20.41) * mm});
            skLineSegment(sketch, "E547", {"start": v(-11.22, -20.41) * mm, "end": v(-37.41, -20.41) * mm});
            skLineSegment(sketch, "E548", {"start": v(12.1, 16.76) * mm, "end": v(12.1, 6.9) * mm});
            skLineSegment(sketch, "E549", {"start": v(12.1, 6.9) * mm, "end": v(20, 4.1) * mm});
            skLineSegment(sketch, "E550", {"start": v(20, 4.1) * mm, "end": v(21.49, 1.6) * mm});
            skLineSegment(sketch, "E551", {"start": v(21.49, 1.6) * mm, "end": v(30.51, 5.43) * mm});
            skLineSegment(sketch, "E552", {"start": v(-2.49, -1.8) * mm, "end": v(10.7, -1.8) * mm});
            skLineSegment(sketch, "E553", {"start": v(10.7, -1.8) * mm, "end": v(15.13, -16.6) * mm});
            skLineSegment(sketch, "E554", {"start": v(15.13, -16.6) * mm, "end": v(7.17, -21.46) * mm});
            skLineSegment(sketch, "E555", {"start": v(7.17, -21.46) * mm, "end": v(22.2, -30.75) * mm});
            skLineSegment(sketch, "E556", {"start": v(22.2, -30.75) * mm, "end": v(22.2, -20.3) * mm});
            skLineSegment(sketch, "E557", {"start": v(22.2, -20.3) * mm, "end": v(33.62, -14.84) * mm});
            skLineSegment(sketch, "E558", {"start": v(33.62, -14.84) * mm, "end": v(31.3, -9.96) * mm});
            skLineSegment(sketch, "E559", {"start": v(31.3, -9.96) * mm, "end": v(30.12, -10.51) * mm});
            skLineSegment(sketch, "E560", {"start": v(30.12, -10.51) * mm, "end": v(23.86, 2.6) * mm});
            skLineSegment(sketch, "E561", {"start": v(14.68, -26.1) * mm, "end": v(14.68, -60.19) * mm});
            skLineSegment(sketch, "E562", {"start": v(14.68, -60.19) * mm, "end": v(26.57, -60.19) * mm});
            skArc(sketch, "E563", {"start": v(37.7, -11.18) * mm, "mid": v(34.3, -11.48) * mm, "end": v(33.62, -14.84) * mm});
            skSolve(sketch);
        }
        {
            var Q0;
            Q0 = qSketchRegion(id + "F2", true);
            var Q1;
            Q1=makeQuery(id+"F2.imprint","IMPRINT",FACE,{"disambiguationData":[TD([[makeQuery(id+"F2.imprint","IMPRINT",EDGE,{"derivedFrom":sQuery(id+"F2.wireOp",EDGE,"E533")}),1.0]])]});
            var Q2;
            Q2=makeQuery(id+"F2.imprint","IMPRINT",FACE,{"disambiguationData":[TD([[makeQuery(id+"F2.imprint","IMPRINT",EDGE,{"derivedFrom":sQuery(id+"F2.wireOp",EDGE,"E526")}),-1.0]])]});
            var Q3;
            Q3=makeQuery(id+"F2.imprint","IMPRINT",FACE,{"disambiguationData":[TD([[makeQuery(id+"F2.imprint","IMPRINT",EDGE,{"derivedFrom":sQuery(id+"F2.wireOp",EDGE,"E526")}),1.0]])]});
            var Q4;
            {var subQ2=sQuery(id+"F2.wireOp",EDGE,"E532");Q4=makeQuery(id+"F2.imprint","IMPRINT",FACE,{"disambiguationData":[TD([[makeQuery(id+"F2.imprint","IMPRINT",EDGE,{"derivedFrom":subQ2}),1.0]])]});}
            var Q5;
            {var subQ6=sQuery(id+"F2.wireOp",EDGE,"E545");Q5=makeQuery(id+"F2.imprint","IMPRINT",FACE,{"disambiguationData":[TD([[makeQuery(id+"F2.imprint","IMPRINT",EDGE,{"derivedFrom":subQ6}),1.0]])]});}
            var Q6;
            {var subQ6=sQuery(id+"F2.wireOp",EDGE,"E556");Q6=makeQuery(id+"F2.imprint","IMPRINT",FACE,{"disambiguationData":[TD([[makeQuery(id+"F2.imprint","IMPRINT",EDGE,{"derivedFrom":subQ6}),-1.0]])]});}
            var Q7;
            Q7=makeQuery(id+"F2.imprint","IMPRINT",FACE,{"disambiguationData":[TD([[makeQuery(id+"F2.imprint","IMPRINT",EDGE,{"derivedFrom":sQuery(id+"F2.wireOp",EDGE,"E558")}),-1.0]])]});
            extrude(context, id + "F3", {"entities" : qUnion([Q0, Q1, Q2, Q3, Q4, Q5, Q6, Q7]), "operationType" : NewBodyOperationType.REMOVE, "oppositeDirection" : true, "depth" : 25 * mm, "offsetDistance" : 25 * mm});
        }
    });
